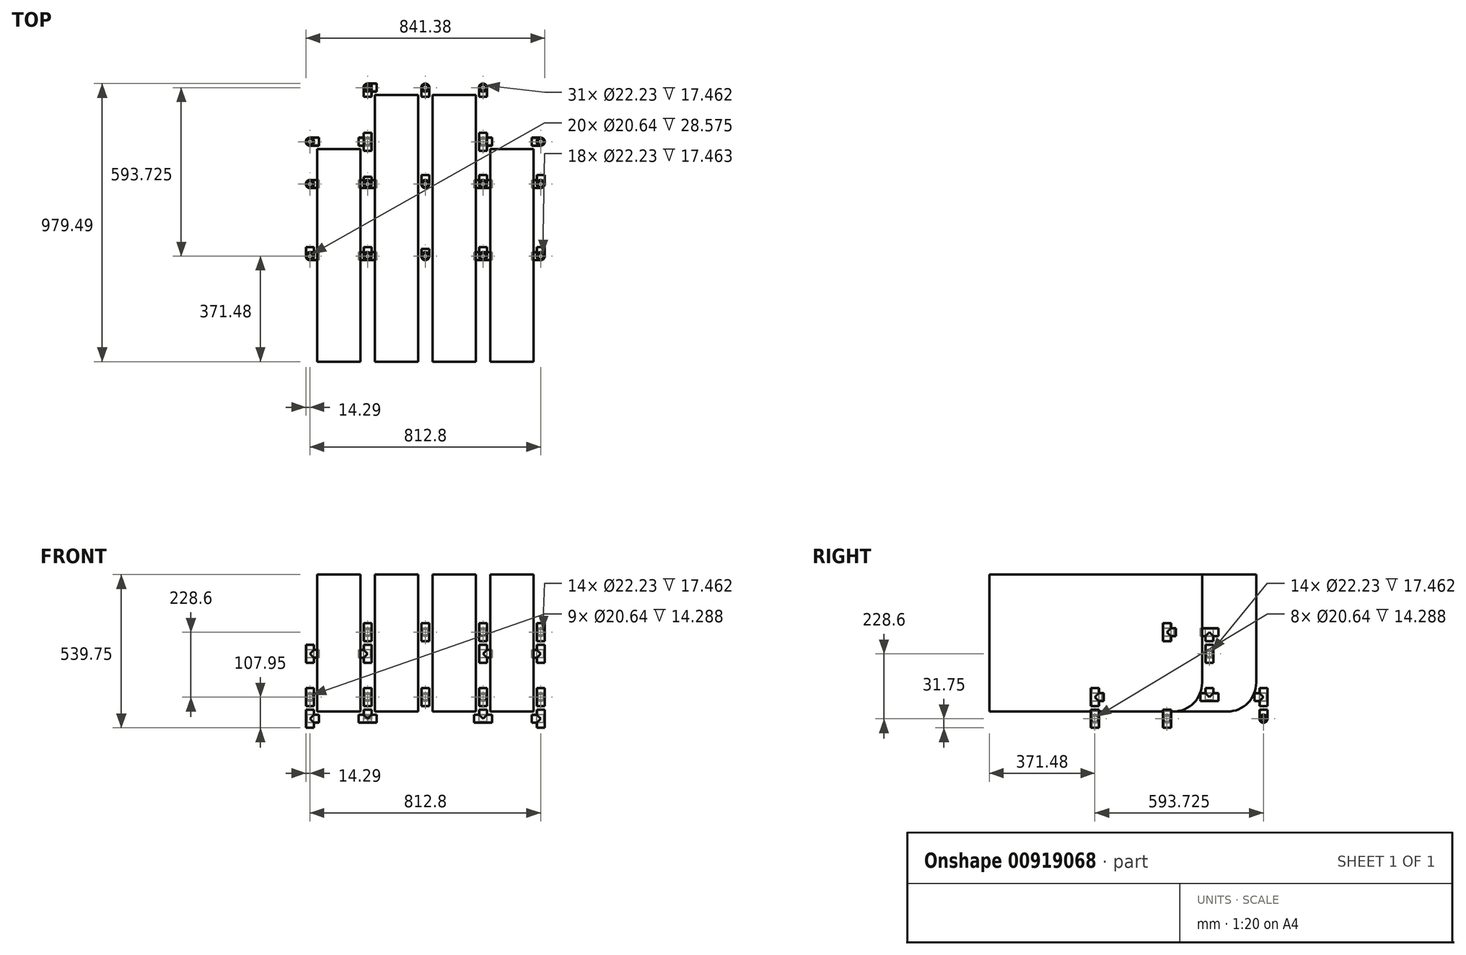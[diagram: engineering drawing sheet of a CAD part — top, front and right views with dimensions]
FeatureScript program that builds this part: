
annotation { "Feature Type Name" : "Feature", "Feature Type Description" : "" }
export const myFeature = defineFeature(function(context is Context, id is Id, definition is map)
    precondition{}
    {
        {
            var Q0;
            Q0=qCreatedBy(makeId("Front.planeOp"),FACE);
            var sketch = newSketch(context, id + "F0", { "sketchPlane" : qUnion([Q0])});
            skLineSegment(sketch, "E0", {"start": v(0, 0) * mm, "end": v(0, 76.2) * mm, "construction": true});
            skLineSegment(sketch, "E1", {"start": v(0, 76.2) * mm, "end": v(0, 381) * mm, "construction": true});
            skLineSegment(sketch, "E2", {"start": v(203.2, 0) * mm, "end": v(203.2, 76.2) * mm, "construction": true});
            skLineSegment(sketch, "E3", {"start": v(203.2, 76.2) * mm, "end": v(203.2, 381) * mm, "construction": true});
            skLineSegment(sketch, "E4", {"start": v(203.2, 381) * mm, "end": v(203.2, 381) * mm});
            skLineSegment(sketch, "E5", {"start": v(406.4, 0) * mm, "end": v(406.4, 76.2) * mm, "construction": true});
            skLineSegment(sketch, "E6", {"start": v(406.4, 76.2) * mm, "end": v(406.4, 381) * mm, "construction": true});
            skLineSegment(sketch, "E7", {"start": v(609.6, 0) * mm, "end": v(609.6, 76.2) * mm, "construction": true});
            skLineSegment(sketch, "E8", {"start": v(609.6, 76.2) * mm, "end": v(609.6, 381) * mm, "construction": true});
            skLineSegment(sketch, "E9", {"start": v(609.6, 381) * mm, "end": v(609.6, 381) * mm});
            skLineSegment(sketch, "E10", {"start": v(812.8, 0) * mm, "end": v(812.8, 76.2) * mm, "construction": true});
            skLineSegment(sketch, "E11", {"start": v(812.8, 76.2) * mm, "end": v(812.8, 381) * mm, "construction": true});
            skLineSegment(sketch, "E12", {"start": v(0, 0) * mm, "end": v(203.2, 0) * mm, "construction": true});
            skLineSegment(sketch, "E13", {"start": v(406.4, 0) * mm, "end": v(609.6, 0) * mm, "construction": true});
            skLineSegment(sketch, "E14", {"start": v(812.8, 0) * mm, "end": v(609.6, 0) * mm, "construction": true});
            skLineSegment(sketch, "E15", {"start": v(406.4, 0) * mm, "end": v(203.2, 0) * mm, "construction": true});
            skCircle(sketch, "E16", {"center": v(406.4, 381) * mm, "radius": 14.29 * mm});
            skCircle(sketch, "E17", {"center": v(406.4, 381) * mm, "radius": 11.11 * mm});
            skCircle(sketch, "E18", {"center": v(406.4, 381) * mm, "radius": 10.32 * mm});
            skCircle(sketch, "E19", {"center": v(406.4, 381) * mm, "radius": 25.4 * mm});
            skCircle(sketch, "E20", {"center": v(609.6, 381) * mm, "radius": 14.29 * mm});
            skCircle(sketch, "E21", {"center": v(609.6, 381) * mm, "radius": 11.11 * mm});
            skCircle(sketch, "E22", {"center": v(609.6, 381) * mm, "radius": 10.32 * mm});
            skCircle(sketch, "E23", {"center": v(609.6, 381) * mm, "radius": 25.4 * mm});
            skCircle(sketch, "E24", {"center": v(203.2, 381) * mm, "radius": 14.29 * mm});
            skCircle(sketch, "E25", {"center": v(203.2, 381) * mm, "radius": 11.11 * mm});
            skCircle(sketch, "E26", {"center": v(203.2, 381) * mm, "radius": 10.32 * mm});
            skCircle(sketch, "E27", {"center": v(203.2, 381) * mm, "radius": 25.4 * mm});
            skCircle(sketch, "E28", {"center": v(406.4, 76.2) * mm, "radius": 14.29 * mm});
            skCircle(sketch, "E29", {"center": v(406.4, 76.2) * mm, "radius": 11.11 * mm});
            skCircle(sketch, "E30", {"center": v(406.4, 76.2) * mm, "radius": 10.32 * mm});
            skCircle(sketch, "E31", {"center": v(406.4, 76.2) * mm, "radius": 25.4 * mm});
            skCircle(sketch, "E32", {"center": v(0, 76.2) * mm, "radius": 14.29 * mm});
            skCircle(sketch, "E33", {"center": v(0, 76.2) * mm, "radius": 11.11 * mm});
            skCircle(sketch, "E34", {"center": v(0, 76.2) * mm, "radius": 10.32 * mm});
            skCircle(sketch, "E35", {"center": v(0, 76.2) * mm, "radius": 25.4 * mm});
            skCircle(sketch, "E36", {"center": v(812.8, 381) * mm, "radius": 14.29 * mm});
            skCircle(sketch, "E37", {"center": v(812.8, 381) * mm, "radius": 11.11 * mm});
            skCircle(sketch, "E38", {"center": v(812.8, 381) * mm, "radius": 10.32 * mm});
            skCircle(sketch, "E39", {"center": v(812.8, 381) * mm, "radius": 25.4 * mm});
            skCircle(sketch, "E40", {"center": v(812.8, 76.2) * mm, "radius": 14.29 * mm});
            skCircle(sketch, "E41", {"center": v(812.8, 76.2) * mm, "radius": 11.11 * mm});
            skCircle(sketch, "E42", {"center": v(812.8, 76.2) * mm, "radius": 10.32 * mm});
            skCircle(sketch, "E43", {"center": v(812.8, 76.2) * mm, "radius": 25.4 * mm});
            skCircle(sketch, "E44", {"center": v(0, 381) * mm, "radius": 14.29 * mm});
            skCircle(sketch, "E45", {"center": v(0, 381) * mm, "radius": 11.11 * mm});
            skCircle(sketch, "E46", {"center": v(0, 381) * mm, "radius": 10.32 * mm});
            skCircle(sketch, "E47", {"center": v(0, 381) * mm, "radius": 25.4 * mm});
            skCircle(sketch, "E48", {"center": v(609.6, 76.2) * mm, "radius": 14.29 * mm});
            skCircle(sketch, "E49", {"center": v(609.6, 76.2) * mm, "radius": 11.11 * mm});
            skCircle(sketch, "E50", {"center": v(609.6, 76.2) * mm, "radius": 10.32 * mm});
            skCircle(sketch, "E51", {"center": v(609.6, 76.2) * mm, "radius": 25.4 * mm});
            skCircle(sketch, "E52", {"center": v(203.2, 76.2) * mm, "radius": 14.29 * mm});
            skCircle(sketch, "E53", {"center": v(203.2, 76.2) * mm, "radius": 11.11 * mm});
            skCircle(sketch, "E54", {"center": v(203.2, 76.2) * mm, "radius": 10.32 * mm});
            skCircle(sketch, "E55", {"center": v(203.2, 76.2) * mm, "radius": 25.4 * mm});
            skSolve(sketch);
        }
        {
            var Q0;
            Q0=qCreatedBy(makeId("Right.planeOp"),FACE);
            var sketch = newSketch(context, id + "F1", { "sketchPlane" : qUnion([Q0])});
            skLineSegment(sketch, "E56", {"start": v(254, 0) * mm, "end": v(254, 76.2) * mm, "construction": true});
            skLineSegment(sketch, "E57", {"start": v(254, 76.2) * mm, "end": v(254, 304.8) * mm, "construction": true});
            skLineSegment(sketch, "E58", {"start": v(254, 304.8) * mm, "end": v(254, 381) * mm, "construction": true});
            skLineSegment(sketch, "E59", {"start": v(254, 381) * mm, "end": v(254, 381) * mm});
            skLineSegment(sketch, "E60", {"start": v(403.23, 0) * mm, "end": v(403.23, 76.2) * mm, "construction": true});
            skLineSegment(sketch, "E61", {"start": v(403.23, 76.2) * mm, "end": v(403.23, 228.6) * mm, "construction": true});
            skLineSegment(sketch, "E62", {"start": v(403.23, 228.6) * mm, "end": v(403.23, 304.8) * mm, "construction": true});
            skCircle(sketch, "E63", {"center": v(0, 0) * mm, "radius": 14.29 * mm});
            skCircle(sketch, "E64", {"center": v(0, 0) * mm, "radius": 11.11 * mm});
            skCircle(sketch, "E65", {"center": v(0, 0) * mm, "radius": 10.32 * mm});
            skLineSegment(sketch, "E66", {"start": v(0, 0) * mm, "end": v(0, 76.2) * mm, "construction": true});
            skLineSegment(sketch, "E67", {"start": v(0, 76.2) * mm, "end": v(0, 381) * mm, "construction": true});
            skCircle(sketch, "E68", {"center": v(403.23, 228.6) * mm, "radius": 14.29 * mm});
            skCircle(sketch, "E69", {"center": v(403.23, 228.6) * mm, "radius": 11.11 * mm});
            skCircle(sketch, "E70", {"center": v(403.23, 228.6) * mm, "radius": 10.32 * mm});
            skCircle(sketch, "E71", {"center": v(403.23, 228.6) * mm, "radius": 25.4 * mm});
            skCircle(sketch, "E72", {"center": v(0, 0) * mm, "radius": 25.4 * mm});
            skCircle(sketch, "E73.1.0.0", {"center": v(254, 0) * mm, "radius": 25.4 * mm});
            skCircle(sketch, "E73.1.0.1", {"center": v(254, 0) * mm, "radius": 11.11 * mm});
            skCircle(sketch, "E73.1.0.2", {"center": v(254, 0) * mm, "radius": 10.32 * mm});
            skCircle(sketch, "E73.1.0.3", {"center": v(254, 0) * mm, "radius": 14.29 * mm});
            skLineSegment(sketch, "E73.direction1", {"start": v(0, 0) * mm, "end": v(254, 0) * mm, "construction": true});
            skLineSegment(sketch, "E74", {"start": v(0, 76.2) * mm, "end": v(254, 76.2) * mm, "construction": true});
            skLineSegment(sketch, "E75", {"start": v(0, 381) * mm, "end": v(254, 381) * mm, "construction": true});
            skLineSegment(sketch, "E76", {"start": v(254, 304.8) * mm, "end": v(403.23, 304.8) * mm, "construction": true});
            skLineSegment(sketch, "E77", {"start": v(254, 76.2) * mm, "end": v(403.23, 76.2) * mm, "construction": true});
            skSolve(sketch);
        }
        {
            var Q0;
            Q0=qCreatedBy(makeId("Right.planeOp"),FACE);
            cPlane(context, id + "F2", {"entities" : qUnion([Q0]), "cplaneType" : CPlaneType.OFFSET, "offset" : 101.6 * mm, "width" : 152.4 * mm, "height" : 152.4 * mm});
        }
        {
            var Q0;
            Q0=qCreatedBy(id+"F2.planeOp",FACE);
            var sketch = newSketch(context, id + "F3", { "sketchPlane" : qUnion([Q0])});
            skLineSegment(sketch, "E78.bottom", {"start": v(377.82, 508) * mm, "end": v(-371.48, 508) * mm});
            skLineSegment(sketch, "E78.top", {"start": v(276.23, 25.4) * mm, "end": v(-371.48, 25.4) * mm});
            skLineSegment(sketch, "E78.left", {"start": v(377.82, 508) * mm, "end": v(377.83, 127) * mm});
            skLineSegment(sketch, "E78.right", {"start": v(-371.48, 508) * mm, "end": v(-371.48, 25.4) * mm});
            skPoint(sketch, "E79.visualSharp", {"position": v(377.83, 25.4) * mm});
            skArc(sketch, "E79.filletArc", {"start": v(276.23, 25.4) * mm, "mid": v(348.07, 55.16) * mm, "end": v(377.83, 127) * mm});
            skSolve(sketch);
        }
        {
            var Q0;
            Q0 = qSketchRegion(id + "F3", true);
            extrude(context, id + "F4", {"entities" : qUnion([Q0]), "endBound" : BoundingType.SYMMETRIC, "depth" : 152.4 * mm, "offsetDistance" : 25.4 * mm});
        }
        {
            var Q0;
            Q0=qCreatedBy(id+"F2.planeOp",FACE);
            cPlane(context, id + "F5", {"entities" : qUnion([Q0]), "cplaneType" : CPlaneType.OFFSET, "offset" : 203.2 * mm, "width" : 152.4 * mm, "height" : 152.4 * mm});
        }
        {
            var Q0;
            Q0=qCreatedBy(id+"F5.planeOp",FACE);
            var sketch = newSketch(context, id + "F6", { "sketchPlane" : qUnion([Q0])});
            skLineSegment(sketch, "E80.bottom", {"start": v(-371.48, 508) * mm, "end": v(568.33, 508) * mm});
            skLineSegment(sketch, "E80.top", {"start": v(-371.48, 25.4) * mm, "end": v(466.73, 25.4) * mm});
            skLineSegment(sketch, "E80.left", {"start": v(-371.48, 508) * mm, "end": v(-371.48, 25.4) * mm});
            skLineSegment(sketch, "E80.right", {"start": v(568.33, 508) * mm, "end": v(568.33, 127) * mm});
            skPoint(sketch, "E81.visualSharp", {"position": v(568.33, 25.4) * mm});
            skArc(sketch, "E81.filletArc", {"start": v(466.73, 25.4) * mm, "mid": v(538.57, 55.16) * mm, "end": v(568.33, 127) * mm});
            skSolve(sketch);
        }
        {
            var Q0;
            Q0 = qSketchRegion(id + "F6", true);
            extrude(context, id + "F7", {"entities" : qUnion([Q0]), "endBound" : BoundingType.SYMMETRIC, "depth" : 152.4 * mm, "offsetDistance" : 25.4 * mm});
        }
        {
            var Q0;
            Q0=qCreatedBy(id+"F5.planeOp",FACE);
            cPlane(context, id + "F8", {"entities" : qUnion([Q0]), "cplaneType" : CPlaneType.OFFSET, "offset" : 203.2 * mm, "width" : 152.4 * mm, "height" : 152.4 * mm});
        }
        {
            var Q0;
            Q0=qCreatedBy(id+"F8.planeOp",FACE);
            var sketch = newSketch(context, id + "F9", { "sketchPlane" : qUnion([Q0])});
            skLineSegment(sketch, "E82.bottom", {"start": v(568.32, 508) * mm, "end": v(-371.48, 508) * mm});
            skLineSegment(sketch, "E82.top", {"start": v(466.72, 25.4) * mm, "end": v(-371.48, 25.4) * mm});
            skLineSegment(sketch, "E82.left", {"start": v(568.32, 508) * mm, "end": v(568.32, 127) * mm});
            skLineSegment(sketch, "E82.right", {"start": v(-371.48, 508) * mm, "end": v(-371.48, 25.4) * mm});
            skPoint(sketch, "E83.visualSharp", {"position": v(568.32, 25.4) * mm});
            skArc(sketch, "E83.filletArc", {"start": v(466.72, 25.4) * mm, "mid": v(538.57, 55.16) * mm, "end": v(568.32, 127) * mm});
            skSolve(sketch);
        }
        {
            var Q0;
            Q0 = qSketchRegion(id + "F9", true);
            extrude(context, id + "F10", {"entities" : qUnion([Q0]), "endBound" : BoundingType.SYMMETRIC, "depth" : 152.4 * mm, "offsetDistance" : 25.4 * mm});
        }
        {
            var Q0;
            Q0=qCreatedBy(id+"F8.planeOp",FACE);
            cPlane(context, id + "F11", {"entities" : qUnion([Q0]), "cplaneType" : CPlaneType.OFFSET, "offset" : 203.2 * mm, "width" : 152.4 * mm, "height" : 152.4 * mm});
        }
        {
            var Q0;
            Q0=qCreatedBy(id+"F11.planeOp",FACE);
            var sketch = newSketch(context, id + "F12", { "sketchPlane" : qUnion([Q0])});
            skLineSegment(sketch, "E84.bottom", {"start": v(377.82, 508) * mm, "end": v(-371.48, 508) * mm});
            skLineSegment(sketch, "E84.top", {"start": v(276.22, 25.4) * mm, "end": v(-371.48, 25.4) * mm});
            skLineSegment(sketch, "E84.left", {"start": v(377.82, 508) * mm, "end": v(377.82, 127) * mm});
            skLineSegment(sketch, "E84.right", {"start": v(-371.48, 508) * mm, "end": v(-371.48, 25.4) * mm});
            skPoint(sketch, "E85.visualSharp", {"position": v(377.82, 25.4) * mm});
            skArc(sketch, "E85.filletArc", {"start": v(276.22, 25.4) * mm, "mid": v(348.07, 55.16) * mm, "end": v(377.82, 127) * mm});
            skSolve(sketch);
        }
        {
            var Q0;
            Q0 = qSketchRegion(id + "F12", true);
            extrude(context, id + "F13", {"entities" : qUnion([Q0]), "endBound" : BoundingType.SYMMETRIC, "depth" : 152.4 * mm, "offsetDistance" : 25.4 * mm});
        }
        {
            var Q0;
            Q0=qCreatedBy(makeId("Right.planeOp"),FACE);
            cPlane(context, id + "F14", {"entities" : qUnion([Q0]), "cplaneType" : CPlaneType.OFFSET, "offset" : 203.2 * mm, "width" : 152.4 * mm, "height" : 152.4 * mm});
        }
        {
            var Q0;
            Q0=qCreatedBy(id+"F14.planeOp",FACE);
            var sketch = newSketch(context, id + "F15", { "sketchPlane" : qUnion([Q0])});
            skLineSegment(sketch, "E86", {"start": v(0, 0) * mm, "end": v(0, 76.2) * mm, "construction": true});
            skLineSegment(sketch, "E87", {"start": v(0, 76.2) * mm, "end": v(0, 381) * mm, "construction": true});
            skLineSegment(sketch, "E88", {"start": v(0, 381) * mm, "end": v(0, 381) * mm});
            skLineSegment(sketch, "E89", {"start": v(254, 0) * mm, "end": v(254, 76.2) * mm, "construction": true});
            skLineSegment(sketch, "E90", {"start": v(254, 76.2) * mm, "end": v(254, 304.8) * mm, "construction": true});
            skLineSegment(sketch, "E91", {"start": v(254, 304.8) * mm, "end": v(254, 381) * mm, "construction": true});
            skLineSegment(sketch, "E92", {"start": v(403.23, 0) * mm, "end": v(403.23, 76.2) * mm, "construction": true});
            skLineSegment(sketch, "E93", {"start": v(403.23, 76.2) * mm, "end": v(403.23, 304.8) * mm, "construction": true});
            skCircle(sketch, "E94", {"center": v(0, 0) * mm, "radius": 14.29 * mm});
            skCircle(sketch, "E95", {"center": v(0, 0) * mm, "radius": 11.11 * mm});
            skCircle(sketch, "E96", {"center": v(0, 0) * mm, "radius": 10.32 * mm});
            skCircle(sketch, "E97", {"center": v(0, 0) * mm, "radius": 25.4 * mm});
            skCircle(sketch, "E98", {"center": v(403.23, 228.6) * mm, "radius": 14.29 * mm});
            skCircle(sketch, "E99", {"center": v(403.23, 228.6) * mm, "radius": 11.11 * mm});
            skCircle(sketch, "E100", {"center": v(403.23, 228.6) * mm, "radius": 10.32 * mm});
            skCircle(sketch, "E101", {"center": v(403.23, 228.6) * mm, "radius": 25.4 * mm});
            skCircle(sketch, "E102", {"center": v(254, 0) * mm, "radius": 14.29 * mm});
            skCircle(sketch, "E103", {"center": v(254, 0) * mm, "radius": 11.11 * mm});
            skCircle(sketch, "E104", {"center": v(254, 0) * mm, "radius": 10.32 * mm});
            skCircle(sketch, "E105", {"center": v(254, 0) * mm, "radius": 25.4 * mm});
            skLineSegment(sketch, "E106", {"start": v(593.73, 0) * mm, "end": v(593.73, 76.2) * mm, "construction": true});
            skLineSegment(sketch, "E107", {"start": v(593.73, 76.2) * mm, "end": v(593.73, 228.6) * mm, "construction": true});
            skLineSegment(sketch, "E108", {"start": v(593.73, 228.6) * mm, "end": v(593.73, 304.8) * mm, "construction": true});
            skCircle(sketch, "E109", {"center": v(593.73, 228.6) * mm, "radius": 14.29 * mm});
            skCircle(sketch, "E110", {"center": v(593.73, 228.6) * mm, "radius": 11.11 * mm});
            skCircle(sketch, "E111", {"center": v(593.73, 228.6) * mm, "radius": 10.32 * mm});
            skCircle(sketch, "E112", {"center": v(593.73, 228.6) * mm, "radius": 25.4 * mm});
            skCircle(sketch, "E113", {"center": v(593.73, 0) * mm, "radius": 14.29 * mm});
            skCircle(sketch, "E114", {"center": v(593.73, 0) * mm, "radius": 11.11 * mm});
            skCircle(sketch, "E115", {"center": v(593.73, 0) * mm, "radius": 10.32 * mm});
            skCircle(sketch, "E116", {"center": v(593.73, 0) * mm, "radius": 25.4 * mm});
            skSolve(sketch);
        }
        {
            var Q0;
            Q0=qCreatedBy(id+"F14.planeOp",FACE);
            cPlane(context, id + "F16", {"entities" : qUnion([Q0]), "cplaneType" : CPlaneType.OFFSET, "offset" : 203.2 * mm, "width" : 152.4 * mm, "height" : 152.4 * mm});
        }
        {
            var Q0;
            Q0=qCreatedBy(id+"F16.planeOp",FACE);
            cPlane(context, id + "F17", {"entities" : qUnion([Q0]), "cplaneType" : CPlaneType.OFFSET, "offset" : 203.2 * mm, "width" : 152.4 * mm, "height" : 152.4 * mm});
        }
        {
            var Q0;
            Q0=qCreatedBy(id+"F17.planeOp",FACE);
            var sketch = newSketch(context, id + "F18", { "sketchPlane" : qUnion([Q0])});
            skLineSegment(sketch, "E117", {"start": v(0, 0) * mm, "end": v(0, 76.2) * mm, "construction": true});
            skLineSegment(sketch, "E118", {"start": v(0, 76.2) * mm, "end": v(0, 381) * mm, "construction": true});
            skLineSegment(sketch, "E119", {"start": v(254, 0) * mm, "end": v(254, 76.2) * mm, "construction": true});
            skLineSegment(sketch, "E120", {"start": v(254, 76.2) * mm, "end": v(254, 304.8) * mm, "construction": true});
            skLineSegment(sketch, "E121", {"start": v(254, 304.8) * mm, "end": v(254, 381) * mm, "construction": true});
            skLineSegment(sketch, "E122", {"start": v(403.23, 0) * mm, "end": v(403.23, 76.2) * mm, "construction": true});
            skLineSegment(sketch, "E123", {"start": v(403.23, 76.2) * mm, "end": v(403.23, 228.6) * mm, "construction": true});
            skLineSegment(sketch, "E124", {"start": v(403.23, 228.6) * mm, "end": v(403.23, 304.8) * mm, "construction": true});
            skLineSegment(sketch, "E125", {"start": v(403.23, 304.8) * mm, "end": v(403.23, 304.8) * mm});
            skLineSegment(sketch, "E126", {"start": v(593.73, 0) * mm, "end": v(593.73, 76.2) * mm, "construction": true});
            skLineSegment(sketch, "E127", {"start": v(593.73, 76.2) * mm, "end": v(593.73, 228.6) * mm, "construction": true});
            skLineSegment(sketch, "E128", {"start": v(593.73, 228.6) * mm, "end": v(593.73, 304.8) * mm, "construction": true});
            skCircle(sketch, "E129", {"center": v(403.23, 228.6) * mm, "radius": 14.29 * mm});
            skCircle(sketch, "E130", {"center": v(403.23, 228.6) * mm, "radius": 11.11 * mm});
            skCircle(sketch, "E131", {"center": v(403.23, 228.6) * mm, "radius": 10.32 * mm});
            skCircle(sketch, "E132", {"center": v(403.23, 228.6) * mm, "radius": 25.4 * mm});
            skCircle(sketch, "E133", {"center": v(593.73, 228.6) * mm, "radius": 14.29 * mm});
            skCircle(sketch, "E134", {"center": v(593.73, 228.6) * mm, "radius": 11.11 * mm});
            skCircle(sketch, "E135", {"center": v(593.73, 228.6) * mm, "radius": 10.32 * mm});
            skCircle(sketch, "E136", {"center": v(593.73, 228.6) * mm, "radius": 25.4 * mm});
            skCircle(sketch, "E137", {"center": v(254, 0) * mm, "radius": 14.29 * mm});
            skCircle(sketch, "E138", {"center": v(254, 0) * mm, "radius": 11.11 * mm});
            skCircle(sketch, "E139", {"center": v(254, 0) * mm, "radius": 10.32 * mm});
            skCircle(sketch, "E140", {"center": v(254, 0) * mm, "radius": 25.4 * mm});
            skCircle(sketch, "E141", {"center": v(0, 0) * mm, "radius": 14.29 * mm});
            skCircle(sketch, "E142", {"center": v(0, 0) * mm, "radius": 11.11 * mm});
            skCircle(sketch, "E143", {"center": v(0, 0) * mm, "radius": 10.32 * mm});
            skCircle(sketch, "E144", {"center": v(0, 0) * mm, "radius": 25.4 * mm});
            skCircle(sketch, "E145", {"center": v(593.73, 0) * mm, "radius": 14.29 * mm});
            skCircle(sketch, "E146", {"center": v(593.73, 0) * mm, "radius": 11.11 * mm});
            skCircle(sketch, "E147", {"center": v(593.73, 0) * mm, "radius": 10.32 * mm});
            skCircle(sketch, "E148", {"center": v(593.73, 0) * mm, "radius": 25.4 * mm});
            skSolve(sketch);
        }
        {
            var Q0;
            Q0=qCreatedBy(id+"F17.planeOp",FACE);
            cPlane(context, id + "F19", {"entities" : qUnion([Q0]), "cplaneType" : CPlaneType.OFFSET, "offset" : 203.2 * mm, "width" : 152.4 * mm, "height" : 152.4 * mm});
        }
        {
            var Q0;
            Q0=qCreatedBy(id+"F19.planeOp",FACE);
            var sketch = newSketch(context, id + "F20", { "sketchPlane" : qUnion([Q0])});
            skLineSegment(sketch, "E149", {"start": v(0, 0) * mm, "end": v(0, 76.2) * mm, "construction": true});
            skLineSegment(sketch, "E150", {"start": v(0, 76.2) * mm, "end": v(0, 381) * mm, "construction": true});
            skLineSegment(sketch, "E151", {"start": v(254, 0) * mm, "end": v(254, 76.2) * mm, "construction": true});
            skLineSegment(sketch, "E152", {"start": v(254, 76.2) * mm, "end": v(254, 304.8) * mm, "construction": true});
            skLineSegment(sketch, "E153", {"start": v(254, 304.8) * mm, "end": v(254, 381) * mm, "construction": true});
            skLineSegment(sketch, "E154", {"start": v(254, 381) * mm, "end": v(254, 381) * mm});
            skLineSegment(sketch, "E155", {"start": v(403.23, 0) * mm, "end": v(403.23, 76.2) * mm, "construction": true});
            skLineSegment(sketch, "E156", {"start": v(403.23, 76.2) * mm, "end": v(403.23, 228.6) * mm, "construction": true});
            skLineSegment(sketch, "E157", {"start": v(403.23, 228.6) * mm, "end": v(403.23, 304.8) * mm, "construction": true});
            skCircle(sketch, "E158", {"center": v(0, 0) * mm, "radius": 14.29 * mm});
            skCircle(sketch, "E159", {"center": v(0, 0) * mm, "radius": 11.11 * mm});
            skCircle(sketch, "E160", {"center": v(0, 0) * mm, "radius": 10.32 * mm});
            skCircle(sketch, "E161", {"center": v(0, 0) * mm, "radius": 25.4 * mm});
            skCircle(sketch, "E162", {"center": v(403.23, 228.6) * mm, "radius": 14.29 * mm});
            skCircle(sketch, "E163", {"center": v(403.23, 228.6) * mm, "radius": 11.11 * mm});
            skCircle(sketch, "E164", {"center": v(403.23, 228.6) * mm, "radius": 10.32 * mm});
            skCircle(sketch, "E165", {"center": v(403.23, 228.6) * mm, "radius": 25.4 * mm});
            skCircle(sketch, "E166", {"center": v(254, 0) * mm, "radius": 14.29 * mm});
            skCircle(sketch, "E167", {"center": v(254, 0) * mm, "radius": 11.11 * mm});
            skCircle(sketch, "E168", {"center": v(254, 0) * mm, "radius": 10.32 * mm});
            skCircle(sketch, "E169", {"center": v(254, 0) * mm, "radius": 25.4 * mm});
            skSolve(sketch);
        }
        {
            var Q0;
            Q0=qCreatedBy(makeId("Front.planeOp"),FACE);
            cPlane(context, id + "F21", {"entities" : qUnion([Q0]), "cplaneType" : CPlaneType.OFFSET, "offset" : 254 * mm, "oppositeDirection" : true, "width" : 152.4 * mm, "height" : 152.4 * mm});
        }
        {
            var Q0;
            Q0=qCreatedBy(id+"F21.planeOp",FACE);
            var sketch = newSketch(context, id + "F22", { "sketchPlane" : qUnion([Q0])});
            skLineSegment(sketch, "E170", {"start": v(0, 0) * mm, "end": v(0, 76.2) * mm, "construction": true});
            skLineSegment(sketch, "E171", {"start": v(0, 76.2) * mm, "end": v(0, 304.8) * mm, "construction": true});
            skLineSegment(sketch, "E172", {"start": v(0, 304.8) * mm, "end": v(0, 381) * mm, "construction": true});
            skLineSegment(sketch, "E173", {"start": v(0, 381) * mm, "end": v(0, 381) * mm});
            skLineSegment(sketch, "E174", {"start": v(203.2, 0) * mm, "end": v(203.2, 76.2) * mm, "construction": true});
            skLineSegment(sketch, "E175", {"start": v(203.2, 76.2) * mm, "end": v(203.2, 304.8) * mm, "construction": true});
            skLineSegment(sketch, "E176", {"start": v(203.2, 304.8) * mm, "end": v(203.2, 381) * mm, "construction": true});
            skLineSegment(sketch, "E177", {"start": v(406.4, 0) * mm, "end": v(406.4, 76.2) * mm, "construction": true});
            skLineSegment(sketch, "E178", {"start": v(406.4, 76.2) * mm, "end": v(406.4, 304.8) * mm, "construction": true});
            skLineSegment(sketch, "E179", {"start": v(406.4, 304.8) * mm, "end": v(406.4, 381) * mm, "construction": true});
            skLineSegment(sketch, "E180", {"start": v(609.6, 0) * mm, "end": v(609.6, 76.2) * mm, "construction": true});
            skLineSegment(sketch, "E181", {"start": v(609.6, 76.2) * mm, "end": v(609.6, 304.8) * mm, "construction": true});
            skLineSegment(sketch, "E182", {"start": v(609.6, 304.8) * mm, "end": v(609.6, 381) * mm, "construction": true});
            skLineSegment(sketch, "E183", {"start": v(812.8, 0) * mm, "end": v(812.8, 76.2) * mm, "construction": true});
            skLineSegment(sketch, "E184", {"start": v(812.8, 76.2) * mm, "end": v(812.8, 304.8) * mm, "construction": true});
            skLineSegment(sketch, "E185", {"start": v(812.8, 304.8) * mm, "end": v(812.8, 381) * mm, "construction": true});
            skCircle(sketch, "E186", {"center": v(406.4, 304.8) * mm, "radius": 14.29 * mm});
            skCircle(sketch, "E187", {"center": v(406.4, 304.8) * mm, "radius": 11.11 * mm});
            skCircle(sketch, "E188", {"center": v(406.4, 304.8) * mm, "radius": 10.32 * mm});
            skCircle(sketch, "E189", {"center": v(406.4, 304.8) * mm, "radius": 25.4 * mm});
            skCircle(sketch, "E190", {"center": v(0, 304.8) * mm, "radius": 14.29 * mm});
            skCircle(sketch, "E191", {"center": v(0, 304.8) * mm, "radius": 11.11 * mm});
            skCircle(sketch, "E192", {"center": v(0, 304.8) * mm, "radius": 10.32 * mm});
            skCircle(sketch, "E193", {"center": v(0, 304.8) * mm, "radius": 25.4 * mm});
            skCircle(sketch, "E194", {"center": v(406.4, 381) * mm, "radius": 14.29 * mm});
            skCircle(sketch, "E195", {"center": v(406.4, 381) * mm, "radius": 11.11 * mm});
            skCircle(sketch, "E196", {"center": v(406.4, 381) * mm, "radius": 10.32 * mm});
            skCircle(sketch, "E197", {"center": v(406.4, 381) * mm, "radius": 25.4 * mm});
            skCircle(sketch, "E198", {"center": v(812.8, 381) * mm, "radius": 14.29 * mm});
            skCircle(sketch, "E199", {"center": v(812.8, 381) * mm, "radius": 11.11 * mm});
            skCircle(sketch, "E200", {"center": v(812.8, 381) * mm, "radius": 10.32 * mm});
            skCircle(sketch, "E201", {"center": v(812.8, 381) * mm, "radius": 25.4 * mm});
            skCircle(sketch, "E202", {"center": v(203.2, 381) * mm, "radius": 14.29 * mm});
            skCircle(sketch, "E203", {"center": v(203.2, 381) * mm, "radius": 11.11 * mm});
            skCircle(sketch, "E204", {"center": v(203.2, 381) * mm, "radius": 10.32 * mm});
            skCircle(sketch, "E205", {"center": v(203.2, 381) * mm, "radius": 25.4 * mm});
            skCircle(sketch, "E206", {"center": v(0, 381) * mm, "radius": 14.29 * mm});
            skCircle(sketch, "E207", {"center": v(0, 381) * mm, "radius": 11.11 * mm});
            skCircle(sketch, "E208", {"center": v(0, 381) * mm, "radius": 10.32 * mm});
            skCircle(sketch, "E209", {"center": v(0, 381) * mm, "radius": 25.4 * mm});
            skCircle(sketch, "E210", {"center": v(812.8, 76.2) * mm, "radius": 14.29 * mm});
            skCircle(sketch, "E211", {"center": v(812.8, 76.2) * mm, "radius": 11.11 * mm});
            skCircle(sketch, "E212", {"center": v(812.8, 76.2) * mm, "radius": 10.32 * mm});
            skCircle(sketch, "E213", {"center": v(812.8, 76.2) * mm, "radius": 25.4 * mm});
            skCircle(sketch, "E214", {"center": v(609.6, 381) * mm, "radius": 14.29 * mm});
            skCircle(sketch, "E215", {"center": v(609.6, 381) * mm, "radius": 11.11 * mm});
            skCircle(sketch, "E216", {"center": v(609.6, 381) * mm, "radius": 10.32 * mm});
            skCircle(sketch, "E217", {"center": v(609.6, 381) * mm, "radius": 25.4 * mm});
            skCircle(sketch, "E218", {"center": v(203.2, 76.2) * mm, "radius": 14.29 * mm});
            skCircle(sketch, "E219", {"center": v(203.2, 76.2) * mm, "radius": 11.11 * mm});
            skCircle(sketch, "E220", {"center": v(203.2, 76.2) * mm, "radius": 10.32 * mm});
            skCircle(sketch, "E221", {"center": v(203.2, 76.2) * mm, "radius": 25.4 * mm});
            skCircle(sketch, "E222", {"center": v(609.6, 76.2) * mm, "radius": 14.29 * mm});
            skCircle(sketch, "E223", {"center": v(609.6, 76.2) * mm, "radius": 11.11 * mm});
            skCircle(sketch, "E224", {"center": v(609.6, 76.2) * mm, "radius": 10.32 * mm});
            skCircle(sketch, "E225", {"center": v(609.6, 76.2) * mm, "radius": 25.4 * mm});
            skCircle(sketch, "E226", {"center": v(609.6, 304.8) * mm, "radius": 14.29 * mm});
            skCircle(sketch, "E227", {"center": v(609.6, 304.8) * mm, "radius": 11.11 * mm});
            skCircle(sketch, "E228", {"center": v(609.6, 304.8) * mm, "radius": 10.32 * mm});
            skCircle(sketch, "E229", {"center": v(609.6, 304.8) * mm, "radius": 25.4 * mm});
            skCircle(sketch, "E230", {"center": v(203.2, 304.8) * mm, "radius": 14.29 * mm});
            skCircle(sketch, "E231", {"center": v(203.2, 304.8) * mm, "radius": 11.11 * mm});
            skCircle(sketch, "E232", {"center": v(203.2, 304.8) * mm, "radius": 10.32 * mm});
            skCircle(sketch, "E233", {"center": v(203.2, 304.8) * mm, "radius": 25.4 * mm});
            skCircle(sketch, "E234", {"center": v(406.4, 76.2) * mm, "radius": 14.29 * mm});
            skCircle(sketch, "E235", {"center": v(406.4, 76.2) * mm, "radius": 11.11 * mm});
            skCircle(sketch, "E236", {"center": v(406.4, 76.2) * mm, "radius": 10.32 * mm});
            skCircle(sketch, "E237", {"center": v(406.4, 76.2) * mm, "radius": 25.4 * mm});
            skCircle(sketch, "E238", {"center": v(0, 76.2) * mm, "radius": 14.29 * mm});
            skCircle(sketch, "E239", {"center": v(0, 76.2) * mm, "radius": 11.11 * mm});
            skCircle(sketch, "E240", {"center": v(0, 76.2) * mm, "radius": 10.32 * mm});
            skCircle(sketch, "E241", {"center": v(0, 76.2) * mm, "radius": 25.4 * mm});
            skCircle(sketch, "E242", {"center": v(812.8, 304.8) * mm, "radius": 14.29 * mm});
            skCircle(sketch, "E243", {"center": v(812.8, 304.8) * mm, "radius": 11.11 * mm});
            skCircle(sketch, "E244", {"center": v(812.8, 304.8) * mm, "radius": 10.32 * mm});
            skCircle(sketch, "E245", {"center": v(812.8, 304.8) * mm, "radius": 25.4 * mm});
            skSolve(sketch);
        }
        {
            var Q0;
            Q0=qCreatedBy(id+"F21.planeOp",FACE);
            cPlane(context, id + "F23", {"entities" : qUnion([Q0]), "cplaneType" : CPlaneType.OFFSET, "offset" : 149.22 * mm, "oppositeDirection" : true, "width" : 152.4 * mm, "height" : 152.4 * mm});
        }
        {
            var Q0;
            Q0=qCreatedBy(id+"F23.planeOp",FACE);
            var sketch = newSketch(context, id + "F24", { "sketchPlane" : qUnion([Q0])});
            skLineSegment(sketch, "E246", {"start": v(0, 0) * mm, "end": v(0, 76.2) * mm, "construction": true});
            skLineSegment(sketch, "E247", {"start": v(0, 76.2) * mm, "end": v(0, 228.6) * mm, "construction": true});
            skLineSegment(sketch, "E248", {"start": v(0, 228.6) * mm, "end": v(0, 304.8) * mm, "construction": true});
            skLineSegment(sketch, "E249", {"start": v(203.2, 0) * mm, "end": v(203.2, 76.2) * mm, "construction": true});
            skLineSegment(sketch, "E250", {"start": v(203.2, 76.2) * mm, "end": v(203.2, 228.6) * mm, "construction": true});
            skLineSegment(sketch, "E251", {"start": v(203.2, 228.6) * mm, "end": v(203.2, 304.8) * mm, "construction": true});
            skLineSegment(sketch, "E252", {"start": v(609.6, 0) * mm, "end": v(609.6, 76.2) * mm, "construction": true});
            skLineSegment(sketch, "E253", {"start": v(609.6, 76.2) * mm, "end": v(609.6, 228.6) * mm, "construction": true});
            skLineSegment(sketch, "E254", {"start": v(609.6, 228.6) * mm, "end": v(609.6, 304.8) * mm, "construction": true});
            skLineSegment(sketch, "E255", {"start": v(812.8, 0) * mm, "end": v(812.8, 76.2) * mm, "construction": true});
            skLineSegment(sketch, "E256", {"start": v(812.8, 76.2) * mm, "end": v(812.8, 228.6) * mm, "construction": true});
            skLineSegment(sketch, "E257", {"start": v(812.8, 228.6) * mm, "end": v(812.8, 304.8) * mm, "construction": true});
            skCircle(sketch, "E258", {"center": v(812.8, 304.8) * mm, "radius": 14.29 * mm});
            skCircle(sketch, "E259", {"center": v(812.8, 304.8) * mm, "radius": 11.11 * mm});
            skCircle(sketch, "E260", {"center": v(812.8, 304.8) * mm, "radius": 10.32 * mm});
            skCircle(sketch, "E261", {"center": v(812.8, 304.8) * mm, "radius": 25.4 * mm});
            skCircle(sketch, "E262", {"center": v(609.6, 304.8) * mm, "radius": 14.29 * mm});
            skCircle(sketch, "E263", {"center": v(609.6, 304.8) * mm, "radius": 11.11 * mm});
            skCircle(sketch, "E264", {"center": v(609.6, 304.8) * mm, "radius": 10.32 * mm});
            skCircle(sketch, "E265", {"center": v(609.6, 304.8) * mm, "radius": 25.4 * mm});
            skCircle(sketch, "E266", {"center": v(0, 76.2) * mm, "radius": 14.29 * mm});
            skCircle(sketch, "E267", {"center": v(0, 76.2) * mm, "radius": 11.11 * mm});
            skCircle(sketch, "E268", {"center": v(0, 76.2) * mm, "radius": 10.32 * mm});
            skCircle(sketch, "E269", {"center": v(0, 76.2) * mm, "radius": 25.4 * mm});
            skCircle(sketch, "E270", {"center": v(0, 304.8) * mm, "radius": 14.29 * mm});
            skCircle(sketch, "E271", {"center": v(0, 304.8) * mm, "radius": 11.11 * mm});
            skCircle(sketch, "E272", {"center": v(0, 304.8) * mm, "radius": 10.32 * mm});
            skCircle(sketch, "E273", {"center": v(0, 304.8) * mm, "radius": 25.4 * mm});
            skCircle(sketch, "E274", {"center": v(203.2, 76.2) * mm, "radius": 14.29 * mm});
            skCircle(sketch, "E275", {"center": v(203.2, 76.2) * mm, "radius": 11.11 * mm});
            skCircle(sketch, "E276", {"center": v(203.2, 76.2) * mm, "radius": 10.32 * mm});
            skCircle(sketch, "E277", {"center": v(203.2, 76.2) * mm, "radius": 25.4 * mm});
            skCircle(sketch, "E278", {"center": v(203.2, 304.8) * mm, "radius": 14.29 * mm});
            skCircle(sketch, "E279", {"center": v(203.2, 304.8) * mm, "radius": 11.11 * mm});
            skCircle(sketch, "E280", {"center": v(203.2, 304.8) * mm, "radius": 10.32 * mm});
            skCircle(sketch, "E281", {"center": v(203.2, 304.8) * mm, "radius": 25.4 * mm});
            skCircle(sketch, "E282", {"center": v(609.6, 76.2) * mm, "radius": 14.29 * mm});
            skCircle(sketch, "E283", {"center": v(609.6, 76.2) * mm, "radius": 11.11 * mm});
            skCircle(sketch, "E284", {"center": v(609.6, 76.2) * mm, "radius": 10.32 * mm});
            skCircle(sketch, "E285", {"center": v(609.6, 76.2) * mm, "radius": 25.4 * mm});
            skCircle(sketch, "E286", {"center": v(812.8, 76.2) * mm, "radius": 14.29 * mm});
            skCircle(sketch, "E287", {"center": v(812.8, 76.2) * mm, "radius": 11.11 * mm});
            skCircle(sketch, "E288", {"center": v(812.8, 76.2) * mm, "radius": 10.32 * mm});
            skCircle(sketch, "E289", {"center": v(812.8, 76.2) * mm, "radius": 25.4 * mm});
            skPoint(sketch, "E290.center.orphan", {"position": v(203.2, 228.6) * mm});
            skPoint(sketch, "E291.center.orphan", {"position": v(609.6, 228.6) * mm});
            skPoint(sketch, "E292.center.orphan", {"position": v(812.8, 228.6) * mm});
            skPoint(sketch, "E293.center.orphan", {"position": v(0, 228.6) * mm});
            skSolve(sketch);
        }
        {
            var Q0;
            Q0=qCreatedBy(makeId("Front.planeOp"),FACE);
            cPlane(context, id + "F25", {"entities" : qUnion([Q0]), "cplaneType" : CPlaneType.OFFSET, "offset" : 593.73 * mm, "oppositeDirection" : true, "width" : 152.4 * mm, "height" : 152.4 * mm});
        }
        {
            var Q0;
            Q0=qCreatedBy(id+"F25.planeOp",FACE);
            var sketch = newSketch(context, id + "F26", { "sketchPlane" : qUnion([Q0])});
            skLineSegment(sketch, "E294", {"start": v(203.2, 0) * mm, "end": v(203.2, 76.2) * mm, "construction": true});
            skLineSegment(sketch, "E295", {"start": v(203.2, 76.2) * mm, "end": v(203.2, 228.6) * mm, "construction": true});
            skLineSegment(sketch, "E296", {"start": v(203.2, 228.6) * mm, "end": v(203.2, 304.8) * mm, "construction": true});
            skLineSegment(sketch, "E297", {"start": v(406.4, 0) * mm, "end": v(406.4, 76.2) * mm, "construction": true});
            skLineSegment(sketch, "E298", {"start": v(406.4, 76.2) * mm, "end": v(406.4, 228.6) * mm, "construction": true});
            skLineSegment(sketch, "E299", {"start": v(406.4, 228.6) * mm, "end": v(406.4, 304.8) * mm, "construction": true});
            skLineSegment(sketch, "E300", {"start": v(609.6, 0) * mm, "end": v(609.6, 76.2) * mm, "construction": true});
            skLineSegment(sketch, "E301", {"start": v(609.6, 76.2) * mm, "end": v(609.6, 228.6) * mm, "construction": true});
            skLineSegment(sketch, "E302", {"start": v(609.6, 228.6) * mm, "end": v(609.6, 304.8) * mm, "construction": true});
            skCircle(sketch, "E303", {"center": v(609.6, 76.2) * mm, "radius": 14.29 * mm});
            skCircle(sketch, "E304", {"center": v(609.6, 76.2) * mm, "radius": 11.11 * mm});
            skCircle(sketch, "E305", {"center": v(609.6, 76.2) * mm, "radius": 10.32 * mm});
            skCircle(sketch, "E306", {"center": v(609.6, 76.2) * mm, "radius": 25.4 * mm});
            skCircle(sketch, "E307", {"center": v(406.4, 304.8) * mm, "radius": 14.29 * mm});
            skCircle(sketch, "E308", {"center": v(406.4, 304.8) * mm, "radius": 11.11 * mm});
            skCircle(sketch, "E309", {"center": v(406.4, 304.8) * mm, "radius": 10.32 * mm});
            skCircle(sketch, "E310", {"center": v(406.4, 304.8) * mm, "radius": 25.4 * mm});
            skCircle(sketch, "E311", {"center": v(203.2, 76.2) * mm, "radius": 14.29 * mm});
            skCircle(sketch, "E312", {"center": v(203.2, 76.2) * mm, "radius": 11.11 * mm});
            skCircle(sketch, "E313", {"center": v(203.2, 76.2) * mm, "radius": 10.32 * mm});
            skCircle(sketch, "E314", {"center": v(203.2, 76.2) * mm, "radius": 25.4 * mm});
            skCircle(sketch, "E315", {"center": v(406.4, 76.2) * mm, "radius": 14.29 * mm});
            skCircle(sketch, "E316", {"center": v(406.4, 76.2) * mm, "radius": 11.11 * mm});
            skCircle(sketch, "E317", {"center": v(406.4, 76.2) * mm, "radius": 10.32 * mm});
            skCircle(sketch, "E318", {"center": v(406.4, 76.2) * mm, "radius": 25.4 * mm});
            skCircle(sketch, "E319", {"center": v(609.6, 304.8) * mm, "radius": 14.29 * mm});
            skCircle(sketch, "E320", {"center": v(609.6, 304.8) * mm, "radius": 11.11 * mm});
            skCircle(sketch, "E321", {"center": v(609.6, 304.8) * mm, "radius": 10.32 * mm});
            skCircle(sketch, "E322", {"center": v(609.6, 304.8) * mm, "radius": 25.4 * mm});
            skCircle(sketch, "E323", {"center": v(203.2, 304.8) * mm, "radius": 14.29 * mm});
            skCircle(sketch, "E324", {"center": v(203.2, 304.8) * mm, "radius": 11.11 * mm});
            skCircle(sketch, "E325", {"center": v(203.2, 304.8) * mm, "radius": 10.32 * mm});
            skCircle(sketch, "E326", {"center": v(203.2, 304.8) * mm, "radius": 25.4 * mm});
            skSolve(sketch);
        }
        {
            var Q0;
            Q0=qCreatedBy(makeId("Top.planeOp"),FACE);
            var sketch = newSketch(context, id + "F27", { "sketchPlane" : qUnion([Q0])});
            skLineSegment(sketch, "E327", {"start": v(0, 0) * mm, "end": v(203.2, 0) * mm, "construction": true});
            skLineSegment(sketch, "E328", {"start": v(203.2, 0) * mm, "end": v(406.4, 0) * mm, "construction": true});
            skLineSegment(sketch, "E329", {"start": v(406.4, 0) * mm, "end": v(609.6, 0) * mm, "construction": true});
            skLineSegment(sketch, "E330", {"start": v(609.6, 0) * mm, "end": v(812.8, 0) * mm, "construction": true});
            skLineSegment(sketch, "E331", {"start": v(0, 254) * mm, "end": v(203.2, 254) * mm, "construction": true});
            skLineSegment(sketch, "E332", {"start": v(203.2, 254) * mm, "end": v(406.4, 254) * mm, "construction": true});
            skLineSegment(sketch, "E333", {"start": v(406.4, 254) * mm, "end": v(609.6, 254) * mm, "construction": true});
            skLineSegment(sketch, "E334", {"start": v(609.6, 254) * mm, "end": v(812.8, 254) * mm, "construction": true});
            skLineSegment(sketch, "E335", {"start": v(0, 403.23) * mm, "end": v(203.2, 403.23) * mm, "construction": true});
            skLineSegment(sketch, "E336", {"start": v(203.2, 403.23) * mm, "end": v(406.4, 403.23) * mm, "construction": true});
            skLineSegment(sketch, "E337", {"start": v(406.4, 403.23) * mm, "end": v(609.6, 403.23) * mm, "construction": true});
            skLineSegment(sketch, "E338", {"start": v(609.6, 403.23) * mm, "end": v(812.8, 403.23) * mm, "construction": true});
            skLineSegment(sketch, "E339", {"start": v(0, 593.73) * mm, "end": v(203.2, 593.73) * mm, "construction": true});
            skLineSegment(sketch, "E340", {"start": v(203.2, 593.73) * mm, "end": v(406.4, 593.73) * mm, "construction": true});
            skLineSegment(sketch, "E341", {"start": v(406.4, 593.73) * mm, "end": v(609.6, 593.73) * mm, "construction": true});
            skLineSegment(sketch, "E342", {"start": v(609.6, 593.73) * mm, "end": v(812.8, 593.73) * mm, "construction": true});
            skCircle(sketch, "E343", {"center": v(812.8, 0) * mm, "radius": 14.29 * mm});
            skCircle(sketch, "E344", {"center": v(812.8, 0) * mm, "radius": 11.11 * mm});
            skCircle(sketch, "E345", {"center": v(812.8, 0) * mm, "radius": 10.32 * mm});
            skCircle(sketch, "E346", {"center": v(812.8, 0) * mm, "radius": 25.4 * mm});
            skCircle(sketch, "E347", {"center": v(406.4, 0) * mm, "radius": 14.29 * mm});
            skCircle(sketch, "E348", {"center": v(406.4, 0) * mm, "radius": 11.11 * mm});
            skCircle(sketch, "E349", {"center": v(406.4, 0) * mm, "radius": 10.32 * mm});
            skCircle(sketch, "E350", {"center": v(406.4, 0) * mm, "radius": 25.4 * mm});
            skCircle(sketch, "E351", {"center": v(203.2, 254) * mm, "radius": 14.29 * mm});
            skCircle(sketch, "E352", {"center": v(203.2, 254) * mm, "radius": 11.11 * mm});
            skCircle(sketch, "E353", {"center": v(203.2, 254) * mm, "radius": 10.32 * mm});
            skCircle(sketch, "E354", {"center": v(203.2, 254) * mm, "radius": 25.4 * mm});
            skCircle(sketch, "E355", {"center": v(203.2, 593.73) * mm, "radius": 14.29 * mm});
            skCircle(sketch, "E356", {"center": v(203.2, 593.73) * mm, "radius": 11.11 * mm});
            skCircle(sketch, "E357", {"center": v(203.2, 593.73) * mm, "radius": 10.32 * mm});
            skCircle(sketch, "E358", {"center": v(203.2, 593.73) * mm, "radius": 25.4 * mm});
            skCircle(sketch, "E359", {"center": v(812.8, 254) * mm, "radius": 14.29 * mm});
            skCircle(sketch, "E360", {"center": v(812.8, 254) * mm, "radius": 11.11 * mm});
            skCircle(sketch, "E361", {"center": v(812.8, 254) * mm, "radius": 10.32 * mm});
            skCircle(sketch, "E362", {"center": v(812.8, 254) * mm, "radius": 25.4 * mm});
            skCircle(sketch, "E363", {"center": v(609.6, 0) * mm, "radius": 14.29 * mm});
            skCircle(sketch, "E364", {"center": v(609.6, 0) * mm, "radius": 11.11 * mm});
            skCircle(sketch, "E365", {"center": v(609.6, 0) * mm, "radius": 10.32 * mm});
            skCircle(sketch, "E366", {"center": v(609.6, 0) * mm, "radius": 25.4 * mm});
            skCircle(sketch, "E367", {"center": v(609.6, 593.73) * mm, "radius": 14.29 * mm});
            skCircle(sketch, "E368", {"center": v(609.6, 593.73) * mm, "radius": 11.11 * mm});
            skCircle(sketch, "E369", {"center": v(609.6, 593.73) * mm, "radius": 10.32 * mm});
            skCircle(sketch, "E370", {"center": v(609.6, 593.73) * mm, "radius": 25.4 * mm});
            skCircle(sketch, "E371", {"center": v(406.4, 254) * mm, "radius": 14.29 * mm});
            skCircle(sketch, "E372", {"center": v(406.4, 254) * mm, "radius": 11.11 * mm});
            skCircle(sketch, "E373", {"center": v(406.4, 254) * mm, "radius": 10.32 * mm});
            skCircle(sketch, "E374", {"center": v(406.4, 254) * mm, "radius": 25.4 * mm});
            skCircle(sketch, "E375", {"center": v(406.4, 593.73) * mm, "radius": 14.29 * mm});
            skCircle(sketch, "E376", {"center": v(406.4, 593.73) * mm, "radius": 11.11 * mm});
            skCircle(sketch, "E377", {"center": v(406.4, 593.73) * mm, "radius": 10.32 * mm});
            skCircle(sketch, "E378", {"center": v(406.4, 593.73) * mm, "radius": 25.4 * mm});
            skCircle(sketch, "E379", {"center": v(609.6, 254) * mm, "radius": 14.29 * mm});
            skCircle(sketch, "E380", {"center": v(609.6, 254) * mm, "radius": 11.11 * mm});
            skCircle(sketch, "E381", {"center": v(609.6, 254) * mm, "radius": 10.32 * mm});
            skCircle(sketch, "E382", {"center": v(609.6, 254) * mm, "radius": 25.4 * mm});
            skCircle(sketch, "E383", {"center": v(203.2, 0) * mm, "radius": 14.29 * mm});
            skCircle(sketch, "E384", {"center": v(203.2, 0) * mm, "radius": 11.11 * mm});
            skCircle(sketch, "E385", {"center": v(203.2, 0) * mm, "radius": 10.32 * mm});
            skCircle(sketch, "E386", {"center": v(203.2, 0) * mm, "radius": 25.4 * mm});
            skCircle(sketch, "E387", {"center": v(0, 254) * mm, "radius": 14.29 * mm});
            skCircle(sketch, "E388", {"center": v(0, 254) * mm, "radius": 11.11 * mm});
            skCircle(sketch, "E389", {"center": v(0, 254) * mm, "radius": 10.32 * mm});
            skCircle(sketch, "E390", {"center": v(0, 254) * mm, "radius": 25.4 * mm});
            skCircle(sketch, "E391", {"center": v(0, 0) * mm, "radius": 14.29 * mm});
            skCircle(sketch, "E392", {"center": v(0, 0) * mm, "radius": 11.11 * mm});
            skCircle(sketch, "E393", {"center": v(0, 0) * mm, "radius": 10.32 * mm});
            skCircle(sketch, "E394", {"center": v(0, 0) * mm, "radius": 25.4 * mm});
            skSolve(sketch);
        }
        {
            var Q0;
            Q0=qCreatedBy(makeId("Top.planeOp"),FACE);
            cPlane(context, id + "F28", {"entities" : qUnion([Q0]), "cplaneType" : CPlaneType.OFFSET, "offset" : 76.2 * mm, "width" : 152.4 * mm, "height" : 152.4 * mm});
        }
        {
            var Q0;
            Q0=qCreatedBy(id+"F28.planeOp",FACE);
            var sketch = newSketch(context, id + "F29", { "sketchPlane" : qUnion([Q0])});
            skLineSegment(sketch, "E395", {"start": v(0, 0) * mm, "end": v(0, 254) * mm, "construction": true});
            skLineSegment(sketch, "E396", {"start": v(0, 254) * mm, "end": v(0, 403.22) * mm, "construction": true});
            skLineSegment(sketch, "E397", {"start": v(203.2, 0) * mm, "end": v(203.2, 254) * mm, "construction": true});
            skLineSegment(sketch, "E398", {"start": v(203.2, 254) * mm, "end": v(203.2, 403.22) * mm, "construction": true});
            skLineSegment(sketch, "E399", {"start": v(203.2, 403.22) * mm, "end": v(203.2, 593.73) * mm, "construction": true});
            skLineSegment(sketch, "E400", {"start": v(406.4, 0) * mm, "end": v(406.4, 254) * mm, "construction": true});
            skLineSegment(sketch, "E401", {"start": v(406.4, 254) * mm, "end": v(406.4, 593.73) * mm, "construction": true});
            skLineSegment(sketch, "E402", {"start": v(609.6, 0) * mm, "end": v(609.6, 254) * mm, "construction": true});
            skLineSegment(sketch, "E403", {"start": v(609.6, 254) * mm, "end": v(609.6, 403.23) * mm, "construction": true});
            skLineSegment(sketch, "E404", {"start": v(609.6, 403.23) * mm, "end": v(609.6, 593.73) * mm, "construction": true});
            skLineSegment(sketch, "E405", {"start": v(812.8, 0) * mm, "end": v(812.8, 254) * mm, "construction": true});
            skLineSegment(sketch, "E406", {"start": v(812.8, 254) * mm, "end": v(812.8, 403.23) * mm, "construction": true});
            skCircle(sketch, "E407", {"center": v(609.6, 254) * mm, "radius": 14.29 * mm});
            skCircle(sketch, "E408", {"center": v(609.6, 254) * mm, "radius": 11.11 * mm});
            skCircle(sketch, "E409", {"center": v(609.6, 254) * mm, "radius": 10.32 * mm});
            skCircle(sketch, "E410", {"center": v(609.6, 254) * mm, "radius": 25.4 * mm});
            skCircle(sketch, "E411", {"center": v(0, 403.23) * mm, "radius": 14.29 * mm});
            skCircle(sketch, "E412", {"center": v(0, 403.23) * mm, "radius": 11.11 * mm});
            skCircle(sketch, "E413", {"center": v(0, 403.23) * mm, "radius": 10.32 * mm});
            skCircle(sketch, "E414", {"center": v(0, 403.23) * mm, "radius": 25.4 * mm});
            skCircle(sketch, "E415", {"center": v(0, 0) * mm, "radius": 14.29 * mm});
            skCircle(sketch, "E416", {"center": v(0, 0) * mm, "radius": 11.11 * mm});
            skCircle(sketch, "E417", {"center": v(0, 0) * mm, "radius": 10.32 * mm});
            skCircle(sketch, "E418", {"center": v(0, 0) * mm, "radius": 25.4 * mm});
            skCircle(sketch, "E419", {"center": v(203.2, 254) * mm, "radius": 14.29 * mm});
            skCircle(sketch, "E420", {"center": v(203.2, 254) * mm, "radius": 11.11 * mm});
            skCircle(sketch, "E421", {"center": v(203.2, 254) * mm, "radius": 10.32 * mm});
            skCircle(sketch, "E422", {"center": v(203.2, 254) * mm, "radius": 25.4 * mm});
            skCircle(sketch, "E423", {"center": v(812.8, 403.23) * mm, "radius": 14.29 * mm});
            skCircle(sketch, "E424", {"center": v(812.8, 403.23) * mm, "radius": 11.11 * mm});
            skCircle(sketch, "E425", {"center": v(812.8, 403.23) * mm, "radius": 10.32 * mm});
            skCircle(sketch, "E426", {"center": v(812.8, 403.23) * mm, "radius": 25.4 * mm});
            skCircle(sketch, "E427", {"center": v(812.8, 254) * mm, "radius": 14.29 * mm});
            skCircle(sketch, "E428", {"center": v(812.8, 254) * mm, "radius": 11.11 * mm});
            skCircle(sketch, "E429", {"center": v(812.8, 254) * mm, "radius": 10.32 * mm});
            skCircle(sketch, "E430", {"center": v(812.8, 254) * mm, "radius": 25.4 * mm});
            skCircle(sketch, "E431", {"center": v(406.4, 0) * mm, "radius": 14.29 * mm});
            skCircle(sketch, "E432", {"center": v(406.4, 0) * mm, "radius": 11.11 * mm});
            skCircle(sketch, "E433", {"center": v(406.4, 0) * mm, "radius": 10.32 * mm});
            skCircle(sketch, "E434", {"center": v(406.4, 0) * mm, "radius": 25.4 * mm});
            skCircle(sketch, "E435", {"center": v(0, 254) * mm, "radius": 14.29 * mm});
            skCircle(sketch, "E436", {"center": v(0, 254) * mm, "radius": 11.11 * mm});
            skCircle(sketch, "E437", {"center": v(0, 254) * mm, "radius": 10.32 * mm});
            skCircle(sketch, "E438", {"center": v(0, 254) * mm, "radius": 25.4 * mm});
            skCircle(sketch, "E439", {"center": v(609.6, 403.23) * mm, "radius": 14.29 * mm});
            skCircle(sketch, "E440", {"center": v(609.6, 403.23) * mm, "radius": 11.11 * mm});
            skCircle(sketch, "E441", {"center": v(609.6, 403.23) * mm, "radius": 10.32 * mm});
            skCircle(sketch, "E442", {"center": v(609.6, 403.23) * mm, "radius": 25.4 * mm});
            skCircle(sketch, "E443", {"center": v(203.2, 0) * mm, "radius": 14.29 * mm});
            skCircle(sketch, "E444", {"center": v(203.2, 0) * mm, "radius": 11.11 * mm});
            skCircle(sketch, "E445", {"center": v(203.2, 0) * mm, "radius": 10.32 * mm});
            skCircle(sketch, "E446", {"center": v(203.2, 0) * mm, "radius": 25.4 * mm});
            skCircle(sketch, "E447", {"center": v(203.2, 403.22) * mm, "radius": 14.29 * mm});
            skCircle(sketch, "E448", {"center": v(203.2, 403.22) * mm, "radius": 11.11 * mm});
            skCircle(sketch, "E449", {"center": v(203.2, 403.22) * mm, "radius": 10.32 * mm});
            skCircle(sketch, "E450", {"center": v(203.2, 403.22) * mm, "radius": 25.4 * mm});
            skCircle(sketch, "E451", {"center": v(203.2, 593.73) * mm, "radius": 14.29 * mm});
            skCircle(sketch, "E452", {"center": v(203.2, 593.73) * mm, "radius": 11.11 * mm});
            skCircle(sketch, "E453", {"center": v(203.2, 593.73) * mm, "radius": 10.32 * mm});
            skCircle(sketch, "E454", {"center": v(203.2, 593.73) * mm, "radius": 25.4 * mm});
            skCircle(sketch, "E455", {"center": v(609.6, 593.73) * mm, "radius": 14.29 * mm});
            skCircle(sketch, "E456", {"center": v(609.6, 593.73) * mm, "radius": 11.11 * mm});
            skCircle(sketch, "E457", {"center": v(609.6, 593.73) * mm, "radius": 10.32 * mm});
            skCircle(sketch, "E458", {"center": v(609.6, 593.73) * mm, "radius": 25.4 * mm});
            skCircle(sketch, "E459", {"center": v(609.6, 0) * mm, "radius": 14.29 * mm});
            skCircle(sketch, "E460", {"center": v(609.6, 0) * mm, "radius": 11.11 * mm});
            skCircle(sketch, "E461", {"center": v(609.6, 0) * mm, "radius": 10.32 * mm});
            skCircle(sketch, "E462", {"center": v(609.6, 0) * mm, "radius": 25.4 * mm});
            skCircle(sketch, "E463", {"center": v(406.4, 254) * mm, "radius": 14.29 * mm});
            skCircle(sketch, "E464", {"center": v(406.4, 254) * mm, "radius": 11.11 * mm});
            skCircle(sketch, "E465", {"center": v(406.4, 254) * mm, "radius": 10.32 * mm});
            skCircle(sketch, "E466", {"center": v(406.4, 254) * mm, "radius": 25.4 * mm});
            skCircle(sketch, "E467", {"center": v(406.4, 593.73) * mm, "radius": 14.29 * mm});
            skCircle(sketch, "E468", {"center": v(406.4, 593.73) * mm, "radius": 11.11 * mm});
            skCircle(sketch, "E469", {"center": v(406.4, 593.73) * mm, "radius": 10.32 * mm});
            skCircle(sketch, "E470", {"center": v(406.4, 593.73) * mm, "radius": 25.4 * mm});
            skCircle(sketch, "E471", {"center": v(812.8, 0) * mm, "radius": 14.29 * mm});
            skCircle(sketch, "E472", {"center": v(812.8, 0) * mm, "radius": 11.11 * mm});
            skCircle(sketch, "E473", {"center": v(812.8, 0) * mm, "radius": 10.32 * mm});
            skCircle(sketch, "E474", {"center": v(812.8, 0) * mm, "radius": 25.4 * mm});
            skSolve(sketch);
        }
        {
            var Q0;
            Q0=qCreatedBy(makeId("Top.planeOp"),FACE);
            cPlane(context, id + "F30", {"entities" : qUnion([Q0]), "cplaneType" : CPlaneType.OFFSET, "offset" : 228.6 * mm, "width" : 152.4 * mm, "height" : 152.4 * mm});
        }
        {
            var Q0;
            Q0=qCreatedBy(id+"F30.planeOp",FACE);
            var sketch = newSketch(context, id + "F31", { "sketchPlane" : qUnion([Q0])});
            skLineSegment(sketch, "E475", {"start": v(0, 403.23) * mm, "end": v(203.2, 403.23) * mm, "construction": true});
            skLineSegment(sketch, "E476", {"start": v(203.2, 593.73) * mm, "end": v(406.4, 593.73) * mm, "construction": true});
            skLineSegment(sketch, "E477", {"start": v(406.4, 593.73) * mm, "end": v(609.6, 593.73) * mm, "construction": true});
            skLineSegment(sketch, "E478", {"start": v(609.6, 403.23) * mm, "end": v(812.8, 403.23) * mm, "construction": true});
            skCircle(sketch, "E479", {"center": v(812.8, 403.23) * mm, "radius": 14.29 * mm});
            skCircle(sketch, "E480", {"center": v(812.8, 403.23) * mm, "radius": 11.11 * mm});
            skCircle(sketch, "E481", {"center": v(812.8, 403.23) * mm, "radius": 10.32 * mm});
            skCircle(sketch, "E482", {"center": v(812.8, 403.23) * mm, "radius": 25.4 * mm});
            skCircle(sketch, "E483", {"center": v(0, 403.23) * mm, "radius": 14.29 * mm});
            skCircle(sketch, "E484", {"center": v(0, 403.23) * mm, "radius": 11.11 * mm});
            skCircle(sketch, "E485", {"center": v(0, 403.23) * mm, "radius": 10.32 * mm});
            skCircle(sketch, "E486", {"center": v(0, 403.23) * mm, "radius": 25.4 * mm});
            skCircle(sketch, "E487", {"center": v(406.4, 593.73) * mm, "radius": 14.29 * mm});
            skCircle(sketch, "E488", {"center": v(406.4, 593.73) * mm, "radius": 11.11 * mm});
            skCircle(sketch, "E489", {"center": v(406.4, 593.73) * mm, "radius": 10.32 * mm});
            skCircle(sketch, "E490", {"center": v(406.4, 593.73) * mm, "radius": 25.4 * mm});
            skCircle(sketch, "E491", {"center": v(203.2, 403.23) * mm, "radius": 14.29 * mm});
            skCircle(sketch, "E492", {"center": v(203.2, 403.23) * mm, "radius": 11.11 * mm});
            skCircle(sketch, "E493", {"center": v(203.2, 403.23) * mm, "radius": 10.32 * mm});
            skCircle(sketch, "E494", {"center": v(203.2, 403.23) * mm, "radius": 25.4 * mm});
            skCircle(sketch, "E495", {"center": v(609.6, 593.73) * mm, "radius": 14.29 * mm});
            skCircle(sketch, "E496", {"center": v(609.6, 593.73) * mm, "radius": 11.11 * mm});
            skCircle(sketch, "E497", {"center": v(609.6, 593.73) * mm, "radius": 10.32 * mm});
            skCircle(sketch, "E498", {"center": v(609.6, 593.73) * mm, "radius": 25.4 * mm});
            skCircle(sketch, "E499", {"center": v(203.2, 593.73) * mm, "radius": 14.29 * mm});
            skCircle(sketch, "E500", {"center": v(203.2, 593.73) * mm, "radius": 11.11 * mm});
            skCircle(sketch, "E501", {"center": v(203.2, 593.73) * mm, "radius": 10.32 * mm});
            skCircle(sketch, "E502", {"center": v(203.2, 593.73) * mm, "radius": 25.4 * mm});
            skCircle(sketch, "E503", {"center": v(609.6, 403.23) * mm, "radius": 14.29 * mm});
            skCircle(sketch, "E504", {"center": v(609.6, 403.23) * mm, "radius": 11.11 * mm});
            skCircle(sketch, "E505", {"center": v(609.6, 403.23) * mm, "radius": 10.32 * mm});
            skCircle(sketch, "E506", {"center": v(609.6, 403.23) * mm, "radius": 25.4 * mm});
            skSolve(sketch);
        }
        {
            var Q0;
            Q0=qCreatedBy(makeId("Top.planeOp"),FACE);
            cPlane(context, id + "F32", {"entities" : qUnion([Q0]), "cplaneType" : CPlaneType.OFFSET, "offset" : 304.8 * mm, "width" : 152.4 * mm, "height" : 152.4 * mm});
        }
        {
            var Q0;
            Q0=qCreatedBy(id+"F32.planeOp",FACE);
            var sketch = newSketch(context, id + "F33", { "sketchPlane" : qUnion([Q0])});
            skLineSegment(sketch, "E507", {"start": v(0, 254) * mm, "end": v(0, 403.23) * mm, "construction": true});
            skLineSegment(sketch, "E508", {"start": v(203.2, 254) * mm, "end": v(203.2, 403.23) * mm, "construction": true});
            skLineSegment(sketch, "E509", {"start": v(203.2, 403.23) * mm, "end": v(203.2, 593.73) * mm, "construction": true});
            skLineSegment(sketch, "E510", {"start": v(406.4, 254) * mm, "end": v(406.4, 403.22) * mm, "construction": true});
            skLineSegment(sketch, "E511", {"start": v(406.4, 403.22) * mm, "end": v(406.4, 593.73) * mm, "construction": true});
            skLineSegment(sketch, "E512", {"start": v(609.6, 254) * mm, "end": v(609.6, 403.23) * mm, "construction": true});
            skLineSegment(sketch, "E513", {"start": v(609.6, 403.23) * mm, "end": v(609.6, 593.73) * mm, "construction": true});
            skLineSegment(sketch, "E514", {"start": v(812.8, 254) * mm, "end": v(812.8, 403.23) * mm, "construction": true});
            skCircle(sketch, "E515", {"center": v(609.6, 254) * mm, "radius": 14.29 * mm});
            skCircle(sketch, "E516", {"center": v(609.6, 254) * mm, "radius": 11.11 * mm});
            skCircle(sketch, "E517", {"center": v(609.6, 254) * mm, "radius": 10.32 * mm});
            skCircle(sketch, "E518", {"center": v(609.6, 254) * mm, "radius": 25.4 * mm});
            skCircle(sketch, "E519", {"center": v(406.4, 254) * mm, "radius": 14.29 * mm});
            skCircle(sketch, "E520", {"center": v(406.4, 254) * mm, "radius": 11.11 * mm});
            skCircle(sketch, "E521", {"center": v(406.4, 254) * mm, "radius": 10.32 * mm});
            skCircle(sketch, "E522", {"center": v(406.4, 254) * mm, "radius": 25.4 * mm});
            skCircle(sketch, "E523", {"center": v(203.2, 403.23) * mm, "radius": 14.29 * mm});
            skCircle(sketch, "E524", {"center": v(203.2, 403.23) * mm, "radius": 11.11 * mm});
            skCircle(sketch, "E525", {"center": v(203.2, 403.23) * mm, "radius": 10.32 * mm});
            skCircle(sketch, "E526", {"center": v(203.2, 403.23) * mm, "radius": 25.4 * mm});
            skCircle(sketch, "E527", {"center": v(406.4, 593.73) * mm, "radius": 14.29 * mm});
            skCircle(sketch, "E528", {"center": v(406.4, 593.73) * mm, "radius": 11.11 * mm});
            skCircle(sketch, "E529", {"center": v(406.4, 593.73) * mm, "radius": 10.32 * mm});
            skCircle(sketch, "E530", {"center": v(406.4, 593.73) * mm, "radius": 25.4 * mm});
            skCircle(sketch, "E531", {"center": v(812.8, 254) * mm, "radius": 14.29 * mm});
            skCircle(sketch, "E532", {"center": v(812.8, 254) * mm, "radius": 11.11 * mm});
            skCircle(sketch, "E533", {"center": v(812.8, 254) * mm, "radius": 10.32 * mm});
            skCircle(sketch, "E534", {"center": v(812.8, 254) * mm, "radius": 25.4 * mm});
            skCircle(sketch, "E535", {"center": v(609.6, 593.73) * mm, "radius": 14.29 * mm});
            skCircle(sketch, "E536", {"center": v(609.6, 593.73) * mm, "radius": 11.11 * mm});
            skCircle(sketch, "E537", {"center": v(609.6, 593.73) * mm, "radius": 10.32 * mm});
            skCircle(sketch, "E538", {"center": v(609.6, 593.73) * mm, "radius": 25.4 * mm});
            skCircle(sketch, "E539", {"center": v(812.8, 403.23) * mm, "radius": 14.29 * mm});
            skCircle(sketch, "E540", {"center": v(812.8, 403.23) * mm, "radius": 11.11 * mm});
            skCircle(sketch, "E541", {"center": v(812.8, 403.23) * mm, "radius": 10.32 * mm});
            skCircle(sketch, "E542", {"center": v(812.8, 403.23) * mm, "radius": 25.4 * mm});
            skCircle(sketch, "E543", {"center": v(0, 403.22) * mm, "radius": 14.29 * mm});
            skCircle(sketch, "E544", {"center": v(0, 403.22) * mm, "radius": 11.11 * mm});
            skCircle(sketch, "E545", {"center": v(0, 403.22) * mm, "radius": 10.32 * mm});
            skCircle(sketch, "E546", {"center": v(0, 403.22) * mm, "radius": 25.4 * mm});
            skCircle(sketch, "E547", {"center": v(203.2, 593.73) * mm, "radius": 14.29 * mm});
            skCircle(sketch, "E548", {"center": v(203.2, 593.73) * mm, "radius": 11.11 * mm});
            skCircle(sketch, "E549", {"center": v(203.2, 593.73) * mm, "radius": 10.32 * mm});
            skCircle(sketch, "E550", {"center": v(203.2, 593.73) * mm, "radius": 25.4 * mm});
            skCircle(sketch, "E551", {"center": v(609.6, 403.23) * mm, "radius": 14.29 * mm});
            skCircle(sketch, "E552", {"center": v(609.6, 403.23) * mm, "radius": 11.11 * mm});
            skCircle(sketch, "E553", {"center": v(609.6, 403.23) * mm, "radius": 10.32 * mm});
            skCircle(sketch, "E554", {"center": v(609.6, 403.23) * mm, "radius": 25.4 * mm});
            skCircle(sketch, "E555", {"center": v(203.2, 254) * mm, "radius": 14.29 * mm});
            skCircle(sketch, "E556", {"center": v(203.2, 254) * mm, "radius": 11.11 * mm});
            skCircle(sketch, "E557", {"center": v(203.2, 254) * mm, "radius": 10.32 * mm});
            skCircle(sketch, "E558", {"center": v(203.2, 254) * mm, "radius": 25.4 * mm});
            skCircle(sketch, "E559", {"center": v(0, 254) * mm, "radius": 14.29 * mm});
            skCircle(sketch, "E560", {"center": v(0, 254) * mm, "radius": 11.11 * mm});
            skCircle(sketch, "E561", {"center": v(0, 254) * mm, "radius": 10.32 * mm});
            skCircle(sketch, "E562", {"center": v(0, 254) * mm, "radius": 25.4 * mm});
            skPoint(sketch, "E563.center.orphan", {"position": v(406.4, 403.23) * mm});
            skSolve(sketch);
        }
        {
            var Q0;
            Q0=qCreatedBy(makeId("Top.planeOp"),FACE);
            cPlane(context, id + "F34", {"entities" : qUnion([Q0]), "cplaneType" : CPlaneType.OFFSET, "offset" : 381 * mm, "width" : 152.4 * mm, "height" : 152.4 * mm});
        }
        {
            var Q0;
            Q0=makeQuery(id+"F1.imprint","IMPRINT",FACE,{"disambiguationData":[TD([[makeQuery(id+"F1.imprint","IMPRINT",EDGE,{"derivedFrom":sQuery(id+"F1.wireOp",EDGE,"E63")}),1.0]])]});
            extrude(context, id + "F35", {"entities" : qUnion([Q0]), "depth" : 31.75 * mm, "offsetDistance" : 25.4 * mm});
        }
        {
            var Q0;
            Q0=makeQuery(id+"F1.imprint","IMPRINT",FACE,{"disambiguationData":[TD([[makeQuery(id+"F1.imprint","IMPRINT",EDGE,{"derivedFrom":sQuery(id+"F1.wireOp",EDGE,"E64")}),1.0]])]});
            extrude(context, id + "F36", {"entities" : qUnion([Q0]), "operationType" : NewBodyOperationType.ADD, "depth" : 14.29 * mm, "offsetDistance" : 25.4 * mm});
        }
        {
            var Q0;
            Q0=makeQuery(id+"F27.imprint","IMPRINT",FACE,{"disambiguationData":[TD([[makeQuery(id+"F27.imprint","IMPRINT",EDGE,{"derivedFrom":sQuery(id+"F27.wireOp",EDGE,"E391")}),1.0]])]});
            extrude(context, id + "F37", {"entities" : qUnion([Q0]), "operationType" : NewBodyOperationType.ADD, "endBound" : BoundingType.SYMMETRIC, "depth" : 63.5 * mm, "offsetDistance" : 25.4 * mm});
        }
        {
            var Q0;
            Q0=makeQuery(id+"F27.imprint","IMPRINT",FACE,{"disambiguationData":[TD([[makeQuery(id+"F27.imprint","IMPRINT",EDGE,{"derivedFrom":sQuery(id+"F27.wireOp",EDGE,"E392")}),1.0]])]});
            extrude(context, id + "F38", {"entities" : qUnion([Q0]), "operationType" : NewBodyOperationType.ADD, "endBound" : BoundingType.SYMMETRIC, "depth" : 28.57 * mm, "offsetDistance" : 25.4 * mm});
        }
        {
            var Q0;
            Q0=makeQuery(id+"F27.imprint","IMPRINT",FACE,{"disambiguationData":[TD([[makeQuery(id+"F27.imprint","IMPRINT",EDGE,{"derivedFrom":sQuery(id+"F27.wireOp",EDGE,"E393")}),1.0]])]});
            extrude(context, id + "F39", {"entities" : qUnion([Q0]), "operationType" : NewBodyOperationType.REMOVE, "endBound" : BoundingType.SYMMETRIC, "oppositeDirection" : true, "depth" : 28.57 * mm, "offsetDistance" : 25.4 * mm});
        }
        {
            var Q0;
            Q0=makeQuery(id+"F1.imprint","IMPRINT",FACE,{"disambiguationData":[TD([[makeQuery(id+"F1.imprint","IMPRINT",EDGE,{"derivedFrom":sQuery(id+"F1.wireOp",EDGE,"E65")}),1.0]])]});
            extrude(context, id + "F40", {"entities" : qUnion([Q0]), "operationType" : NewBodyOperationType.REMOVE, "depth" : 14.29 * mm, "offsetDistance" : 25.4 * mm});
        }
        {
            var Q0;
            Q0=makeQuery(id+"F1.imprint","IMPRINT",FACE,{"disambiguationData":[TD([[makeQuery(id+"F1.imprint","IMPRINT",EDGE,{"derivedFrom":sQuery(id+"F1.wireOp",EDGE,"E73.1.0.1")}),1.0]])]});
            extrude(context, id + "F41", {"entities" : qUnion([Q0]), "depth" : 14.29 * mm, "offsetDistance" : 25.4 * mm});
        }
        {
            var Q0;
            Q0=makeQuery(id+"F1.imprint","IMPRINT",FACE,{"disambiguationData":[TD([[makeQuery(id+"F1.imprint","IMPRINT",EDGE,{"derivedFrom":sQuery(id+"F1.wireOp",EDGE,"E73.1.0.1")}),-1.0]])]});
            extrude(context, id + "F42", {"entities" : qUnion([Q0]), "operationType" : NewBodyOperationType.ADD, "depth" : 31.75 * mm, "offsetDistance" : 25.4 * mm});
        }
        {
            var Q0;
            Q0=makeQuery(id+"F27.imprint","IMPRINT",FACE,{"disambiguationData":[TD([[makeQuery(id+"F27.imprint","IMPRINT",EDGE,{"derivedFrom":sQuery(id+"F27.wireOp",EDGE,"E388")}),1.0]])]});
            extrude(context, id + "F43", {"entities" : qUnion([Q0]), "operationType" : NewBodyOperationType.ADD, "endBound" : BoundingType.SYMMETRIC, "depth" : 28.57 * mm, "offsetDistance" : 25.4 * mm});
        }
        {
            var Q0;
            Q0=makeQuery(id+"F27.imprint","IMPRINT",FACE,{"disambiguationData":[TD([[makeQuery(id+"F27.imprint","IMPRINT",EDGE,{"derivedFrom":sQuery(id+"F27.wireOp",EDGE,"E387")}),1.0]])]});
            extrude(context, id + "F44", {"entities" : qUnion([Q0]), "operationType" : NewBodyOperationType.ADD, "endBound" : BoundingType.SYMMETRIC, "depth" : 63.5 * mm, "offsetDistance" : 25.4 * mm});
        }
        {
            var Q0;
            Q0=makeQuery(id+"F27.imprint","IMPRINT",FACE,{"disambiguationData":[TD([[makeQuery(id+"F27.imprint","IMPRINT",EDGE,{"derivedFrom":sQuery(id+"F27.wireOp",EDGE,"E389")}),1.0]])]});
            extrude(context, id + "F45", {"entities" : qUnion([Q0]), "operationType" : NewBodyOperationType.REMOVE, "endBound" : BoundingType.SYMMETRIC, "oppositeDirection" : true, "depth" : 28.57 * mm, "offsetDistance" : 25.4 * mm});
        }
        {
            var Q0;
            Q0=makeQuery(id+"F1.imprint","IMPRINT",FACE,{"disambiguationData":[TD([[makeQuery(id+"F1.imprint","IMPRINT",EDGE,{"derivedFrom":sQuery(id+"F1.wireOp",EDGE,"E73.1.0.2")}),1.0]])]});
            extrude(context, id + "F46", {"entities" : qUnion([Q0]), "operationType" : NewBodyOperationType.REMOVE, "depth" : 14.29 * mm, "offsetDistance" : 25.4 * mm});
        }
        {
            var Q0;
            Q0=makeQuery(id+"F1.imprint","IMPRINT",FACE,{"disambiguationData":[TD([[makeQuery(id+"F1.imprint","IMPRINT",EDGE,{"derivedFrom":sQuery(id+"F1.wireOp",EDGE,"E69")}),1.0]])]});
            extrude(context, id + "F47", {"entities" : qUnion([Q0]), "depth" : 14.29 * mm, "offsetDistance" : 25.4 * mm});
        }
        {
            var Q0;
            Q0=makeQuery(id+"F1.imprint","IMPRINT",FACE,{"disambiguationData":[TD([[makeQuery(id+"F1.imprint","IMPRINT",EDGE,{"derivedFrom":sQuery(id+"F1.wireOp",EDGE,"E68")}),1.0]])]});
            extrude(context, id + "F48", {"entities" : qUnion([Q0]), "operationType" : NewBodyOperationType.ADD, "depth" : 31.75 * mm, "offsetDistance" : 25.4 * mm});
        }
        {
            var Q0;
            Q0=makeQuery(id+"F31.imprint","IMPRINT",FACE,{"disambiguationData":[TD([[makeQuery(id+"F31.imprint","IMPRINT",EDGE,{"derivedFrom":sQuery(id+"F31.wireOp",EDGE,"E485")}),1.0]])]});
            extrude(context, id + "F49", {"entities" : qUnion([Q0]), "operationType" : NewBodyOperationType.REMOVE, "endBound" : BoundingType.SYMMETRIC, "oppositeDirection" : true, "depth" : 28.57 * mm, "offsetDistance" : 25.4 * mm});
        }
        {
            var Q0;
            Q0=makeQuery(id+"F31.imprint","IMPRINT",FACE,{"disambiguationData":[TD([[makeQuery(id+"F31.imprint","IMPRINT",EDGE,{"derivedFrom":sQuery(id+"F31.wireOp",EDGE,"E484")}),1.0]])]});
            extrude(context, id + "F50", {"entities" : qUnion([Q0]), "operationType" : NewBodyOperationType.ADD, "endBound" : BoundingType.SYMMETRIC, "depth" : 28.57 * mm, "offsetDistance" : 25.4 * mm});
        }
        {
            var Q0;
            Q0=makeQuery(id+"F31.imprint","IMPRINT",FACE,{"disambiguationData":[TD([[makeQuery(id+"F31.imprint","IMPRINT",EDGE,{"derivedFrom":sQuery(id+"F31.wireOp",EDGE,"E483")}),1.0]])]});
            extrude(context, id + "F51", {"entities" : qUnion([Q0]), "operationType" : NewBodyOperationType.ADD, "endBound" : BoundingType.SYMMETRIC, "depth" : 63.5 * mm, "offsetDistance" : 25.4 * mm});
        }
        {
            var Q0;
            Q0=makeQuery(id+"F1.imprint","IMPRINT",FACE,{"disambiguationData":[TD([[makeQuery(id+"F1.imprint","IMPRINT",EDGE,{"derivedFrom":sQuery(id+"F1.wireOp",EDGE,"E70")}),1.0]])]});
            extrude(context, id + "F52", {"entities" : qUnion([Q0]), "operationType" : NewBodyOperationType.REMOVE, "depth" : 14.29 * mm, "offsetDistance" : 25.4 * mm});
        }
        {
            var Q0;
            Q0=makeQuery(id+"F0.imprint","IMPRINT",FACE,{"disambiguationData":[TD([[makeQuery(id+"F0.imprint","IMPRINT",EDGE,{"derivedFrom":sQuery(id+"F0.wireOp",EDGE,"E33")}),1.0]])]});
            extrude(context, id + "F53", {"entities" : qUnion([Q0]), "oppositeDirection" : true, "depth" : 14.29 * mm, "offsetDistance" : 25.4 * mm});
        }
        {
            var Q0;
            Q0=makeQuery(id+"F0.imprint","IMPRINT",FACE,{"disambiguationData":[TD([[makeQuery(id+"F0.imprint","IMPRINT",EDGE,{"derivedFrom":sQuery(id+"F0.wireOp",EDGE,"E32")}),1.0]])]});
            extrude(context, id + "F54", {"entities" : qUnion([Q0]), "operationType" : NewBodyOperationType.ADD, "oppositeDirection" : true, "depth" : 31.75 * mm, "offsetDistance" : 25.4 * mm});
        }
        {
            var Q0;
            Q0=makeQuery(id+"F29.imprint","IMPRINT",FACE,{"disambiguationData":[TD([[makeQuery(id+"F29.imprint","IMPRINT",EDGE,{"derivedFrom":sQuery(id+"F29.wireOp",EDGE,"E417")}),1.0]])]});
            extrude(context, id + "F55", {"entities" : qUnion([Q0]), "operationType" : NewBodyOperationType.REMOVE, "endBound" : BoundingType.SYMMETRIC, "oppositeDirection" : true, "depth" : 28.57 * mm, "offsetDistance" : 25.4 * mm});
        }
        {
            var Q0;
            Q0=makeQuery(id+"F29.imprint","IMPRINT",FACE,{"disambiguationData":[TD([[makeQuery(id+"F29.imprint","IMPRINT",EDGE,{"derivedFrom":sQuery(id+"F29.wireOp",EDGE,"E416")}),1.0]])]});
            extrude(context, id + "F56", {"entities" : qUnion([Q0]), "operationType" : NewBodyOperationType.ADD, "endBound" : BoundingType.SYMMETRIC, "depth" : 28.57 * mm, "offsetDistance" : 25.4 * mm});
        }
        {
            var Q0;
            Q0=makeQuery(id+"F29.imprint","IMPRINT",FACE,{"disambiguationData":[TD([[makeQuery(id+"F29.imprint","IMPRINT",EDGE,{"derivedFrom":sQuery(id+"F29.wireOp",EDGE,"E415")}),1.0]])]});
            extrude(context, id + "F57", {"entities" : qUnion([Q0]), "operationType" : NewBodyOperationType.ADD, "endBound" : BoundingType.SYMMETRIC, "depth" : 63.5 * mm, "offsetDistance" : 25.4 * mm});
        }
        {
            var Q0;
            Q0=makeQuery(id+"F0.imprint","IMPRINT",FACE,{"disambiguationData":[TD([[makeQuery(id+"F0.imprint","IMPRINT",EDGE,{"derivedFrom":sQuery(id+"F0.wireOp",EDGE,"E34")}),1.0]])]});
            extrude(context, id + "F58", {"entities" : qUnion([Q0]), "operationType" : NewBodyOperationType.REMOVE, "oppositeDirection" : true, "depth" : 14.29 * mm, "offsetDistance" : 25.4 * mm});
        }
        {
            var Q0;
            Q0=makeQuery(id+"F27.imprint","IMPRINT",FACE,{"disambiguationData":[TD([[makeQuery(id+"F27.imprint","IMPRINT",EDGE,{"derivedFrom":sQuery(id+"F27.wireOp",EDGE,"E384")}),1.0]])]});
            extrude(context, id + "F59", {"entities" : qUnion([Q0]), "depth" : 14.29 * mm, "offsetDistance" : 25.4 * mm});
        }
        {
            var Q0;
            Q0=makeQuery(id+"F27.imprint","IMPRINT",FACE,{"disambiguationData":[TD([[makeQuery(id+"F27.imprint","IMPRINT",EDGE,{"derivedFrom":sQuery(id+"F27.wireOp",EDGE,"E383")}),1.0]])]});
            extrude(context, id + "F60", {"entities" : qUnion([Q0]), "operationType" : NewBodyOperationType.ADD, "depth" : 31.75 * mm, "offsetDistance" : 25.4 * mm});
        }
        {
            var Q0;
            Q0=makeQuery(id+"F15.imprint","IMPRINT",FACE,{"disambiguationData":[TD([[makeQuery(id+"F15.imprint","IMPRINT",EDGE,{"derivedFrom":sQuery(id+"F15.wireOp",EDGE,"E96")}),1.0]])]});
            extrude(context, id + "F61", {"entities" : qUnion([Q0]), "operationType" : NewBodyOperationType.REMOVE, "endBound" : BoundingType.SYMMETRIC, "depth" : 28.57 * mm, "offsetDistance" : 25.4 * mm});
        }
        {
            var Q0;
            Q0=makeQuery(id+"F15.imprint","IMPRINT",FACE,{"disambiguationData":[TD([[makeQuery(id+"F15.imprint","IMPRINT",EDGE,{"derivedFrom":sQuery(id+"F15.wireOp",EDGE,"E95")}),1.0]])]});
            extrude(context, id + "F62", {"entities" : qUnion([Q0]), "operationType" : NewBodyOperationType.ADD, "endBound" : BoundingType.SYMMETRIC, "depth" : 28.57 * mm, "offsetDistance" : 25.4 * mm});
        }
        {
            var Q0;
            Q0=makeQuery(id+"F15.imprint","IMPRINT",FACE,{"disambiguationData":[TD([[makeQuery(id+"F15.imprint","IMPRINT",EDGE,{"derivedFrom":sQuery(id+"F15.wireOp",EDGE,"E94")}),1.0]])]});
            extrude(context, id + "F63", {"entities" : qUnion([Q0]), "operationType" : NewBodyOperationType.ADD, "endBound" : BoundingType.SYMMETRIC, "depth" : 63.5 * mm, "offsetDistance" : 25.4 * mm});
        }
        {
            var Q0;
            Q0=makeQuery(id+"F27.imprint","IMPRINT",FACE,{"disambiguationData":[TD([[makeQuery(id+"F27.imprint","IMPRINT",EDGE,{"derivedFrom":sQuery(id+"F27.wireOp",EDGE,"E385")}),1.0]])]});
            extrude(context, id + "F64", {"entities" : qUnion([Q0]), "operationType" : NewBodyOperationType.REMOVE, "depth" : 25.4 * mm, "offsetDistance" : 25.4 * mm});
        }
        {
            var Q0;
            Q0=makeQuery(id+"F0.imprint","IMPRINT",FACE,{"disambiguationData":[TD([[makeQuery(id+"F0.imprint","IMPRINT",EDGE,{"derivedFrom":sQuery(id+"F0.wireOp",EDGE,"E53")}),1.0]])]});
            extrude(context, id + "F65", {"entities" : qUnion([Q0]), "oppositeDirection" : true, "depth" : 14.29 * mm, "offsetDistance" : 25.4 * mm});
        }
        {
            var Q0;
            Q0=makeQuery(id+"F0.imprint","IMPRINT",FACE,{"disambiguationData":[TD([[makeQuery(id+"F0.imprint","IMPRINT",EDGE,{"derivedFrom":sQuery(id+"F0.wireOp",EDGE,"E52")}),1.0]])]});
            extrude(context, id + "F66", {"entities" : qUnion([Q0]), "operationType" : NewBodyOperationType.ADD, "oppositeDirection" : true, "depth" : 31.75 * mm, "offsetDistance" : 25.4 * mm});
        }
        {
            var Q0;
            Q0=makeQuery(id+"F29.imprint","IMPRINT",FACE,{"disambiguationData":[TD([[makeQuery(id+"F29.imprint","IMPRINT",EDGE,{"derivedFrom":sQuery(id+"F29.wireOp",EDGE,"E445")}),1.0]])]});
            extrude(context, id + "F67", {"entities" : qUnion([Q0]), "operationType" : NewBodyOperationType.REMOVE, "endBound" : BoundingType.SYMMETRIC, "oppositeDirection" : true, "depth" : 28.57 * mm, "offsetDistance" : 25.4 * mm});
        }
        {
            var Q0;
            Q0=makeQuery(id+"F29.imprint","IMPRINT",FACE,{"disambiguationData":[TD([[makeQuery(id+"F29.imprint","IMPRINT",EDGE,{"derivedFrom":sQuery(id+"F29.wireOp",EDGE,"E444")}),1.0]])]});
            extrude(context, id + "F68", {"entities" : qUnion([Q0]), "operationType" : NewBodyOperationType.ADD, "endBound" : BoundingType.SYMMETRIC, "depth" : 28.57 * mm, "offsetDistance" : 25.4 * mm});
        }
        {
            var Q0;
            Q0=makeQuery(id+"F29.imprint","IMPRINT",FACE,{"disambiguationData":[TD([[makeQuery(id+"F29.imprint","IMPRINT",EDGE,{"derivedFrom":sQuery(id+"F29.wireOp",EDGE,"E443")}),1.0]])]});
            extrude(context, id + "F69", {"entities" : qUnion([Q0]), "operationType" : NewBodyOperationType.ADD, "endBound" : BoundingType.SYMMETRIC, "depth" : 63.5 * mm, "offsetDistance" : 25.4 * mm});
        }
        {
            var Q0;
            Q0=makeQuery(id+"F0.imprint","IMPRINT",FACE,{"disambiguationData":[TD([[makeQuery(id+"F0.imprint","IMPRINT",EDGE,{"derivedFrom":sQuery(id+"F0.wireOp",EDGE,"E54")}),1.0]])]});
            extrude(context, id + "F70", {"entities" : qUnion([Q0]), "operationType" : NewBodyOperationType.REMOVE, "oppositeDirection" : true, "depth" : 14.29 * mm, "offsetDistance" : 25.4 * mm});
        }
        {
            var Q0;
            Q0=makeQuery(id+"F0.imprint","IMPRINT",FACE,{"disambiguationData":[TD([[makeQuery(id+"F0.imprint","IMPRINT",EDGE,{"derivedFrom":sQuery(id+"F0.wireOp",EDGE,"E29")}),1.0]])]});
            extrude(context, id + "F71", {"entities" : qUnion([Q0]), "oppositeDirection" : true, "depth" : 14.29 * mm, "offsetDistance" : 25.4 * mm});
        }
        {
            var Q0;
            Q0=makeQuery(id+"F0.imprint","IMPRINT",FACE,{"disambiguationData":[TD([[makeQuery(id+"F0.imprint","IMPRINT",EDGE,{"derivedFrom":sQuery(id+"F0.wireOp",EDGE,"E28")}),1.0]])]});
            extrude(context, id + "F72", {"entities" : qUnion([Q0]), "operationType" : NewBodyOperationType.ADD, "oppositeDirection" : true, "depth" : 25.4 * mm, "offsetDistance" : 25.4 * mm});
        }
        {
            var Q0;
            Q0=makeQuery(id+"F29.imprint","IMPRINT",FACE,{"disambiguationData":[TD([[makeQuery(id+"F29.imprint","IMPRINT",EDGE,{"derivedFrom":sQuery(id+"F29.wireOp",EDGE,"E433")}),1.0]])]});
            extrude(context, id + "F73", {"entities" : qUnion([Q0]), "operationType" : NewBodyOperationType.REMOVE, "endBound" : BoundingType.SYMMETRIC, "oppositeDirection" : true, "depth" : 28.57 * mm, "offsetDistance" : 25.4 * mm});
        }
        {
            var Q0;
            Q0=makeQuery(id+"F29.imprint","IMPRINT",FACE,{"disambiguationData":[TD([[makeQuery(id+"F29.imprint","IMPRINT",EDGE,{"derivedFrom":sQuery(id+"F29.wireOp",EDGE,"E432")}),1.0]])]});
            extrude(context, id + "F74", {"entities" : qUnion([Q0]), "operationType" : NewBodyOperationType.ADD, "endBound" : BoundingType.SYMMETRIC, "depth" : 28.57 * mm, "offsetDistance" : 25.4 * mm});
        }
        {
            var Q0;
            Q0=makeQuery(id+"F29.imprint","IMPRINT",FACE,{"disambiguationData":[TD([[makeQuery(id+"F29.imprint","IMPRINT",EDGE,{"derivedFrom":sQuery(id+"F29.wireOp",EDGE,"E431")}),1.0]])]});
            extrude(context, id + "F75", {"entities" : qUnion([Q0]), "operationType" : NewBodyOperationType.ADD, "endBound" : BoundingType.SYMMETRIC, "depth" : 63.5 * mm, "offsetDistance" : 25.4 * mm});
        }
        {
            var Q0;
            Q0=makeQuery(id+"F0.imprint","IMPRINT",FACE,{"disambiguationData":[TD([[makeQuery(id+"F0.imprint","IMPRINT",EDGE,{"derivedFrom":sQuery(id+"F0.wireOp",EDGE,"E30")}),1.0]])]});
            extrude(context, id + "F76", {"entities" : qUnion([Q0]), "operationType" : NewBodyOperationType.REMOVE, "oppositeDirection" : true, "depth" : 14.29 * mm, "offsetDistance" : 25.4 * mm});
        }
        {
            var Q0;
            Q0=makeQuery(id+"F27.imprint","IMPRINT",FACE,{"disambiguationData":[TD([[makeQuery(id+"F27.imprint","IMPRINT",EDGE,{"derivedFrom":sQuery(id+"F27.wireOp",EDGE,"E364")}),1.0]])]});
            extrude(context, id + "F77", {"entities" : qUnion([Q0]), "depth" : 14.29 * mm, "offsetDistance" : 25.4 * mm});
        }
        {
            var Q0;
            Q0=makeQuery(id+"F27.imprint","IMPRINT",FACE,{"disambiguationData":[TD([[makeQuery(id+"F27.imprint","IMPRINT",EDGE,{"derivedFrom":sQuery(id+"F27.wireOp",EDGE,"E363")}),1.0]])]});
            extrude(context, id + "F78", {"entities" : qUnion([Q0]), "operationType" : NewBodyOperationType.ADD, "depth" : 31.75 * mm, "offsetDistance" : 25.4 * mm});
        }
        {
            var Q0;
            Q0=makeQuery(id+"F18.imprint","IMPRINT",FACE,{"disambiguationData":[TD([[makeQuery(id+"F18.imprint","IMPRINT",EDGE,{"derivedFrom":sQuery(id+"F18.wireOp",EDGE,"E143")}),1.0]])]});
            extrude(context, id + "F79", {"entities" : qUnion([Q0]), "operationType" : NewBodyOperationType.REMOVE, "endBound" : BoundingType.SYMMETRIC, "oppositeDirection" : true, "depth" : 28.57 * mm, "offsetDistance" : 25.4 * mm});
        }
        {
            var Q0;
            Q0=makeQuery(id+"F18.imprint","IMPRINT",FACE,{"disambiguationData":[TD([[makeQuery(id+"F18.imprint","IMPRINT",EDGE,{"derivedFrom":sQuery(id+"F18.wireOp",EDGE,"E142")}),1.0]])]});
            extrude(context, id + "F80", {"entities" : qUnion([Q0]), "operationType" : NewBodyOperationType.ADD, "endBound" : BoundingType.SYMMETRIC, "depth" : 28.57 * mm, "offsetDistance" : 25.4 * mm});
        }
        {
            var Q0;
            Q0=makeQuery(id+"F18.imprint","IMPRINT",FACE,{"disambiguationData":[TD([[makeQuery(id+"F18.imprint","IMPRINT",EDGE,{"derivedFrom":sQuery(id+"F18.wireOp",EDGE,"E141")}),1.0]])]});
            extrude(context, id + "F81", {"entities" : qUnion([Q0]), "operationType" : NewBodyOperationType.ADD, "endBound" : BoundingType.SYMMETRIC, "depth" : 63.5 * mm, "offsetDistance" : 25.4 * mm});
        }
        {
            var Q0;
            Q0=makeQuery(id+"F27.imprint","IMPRINT",FACE,{"disambiguationData":[TD([[makeQuery(id+"F27.imprint","IMPRINT",EDGE,{"derivedFrom":sQuery(id+"F27.wireOp",EDGE,"E365")}),1.0]])]});
            extrude(context, id + "F82", {"entities" : qUnion([Q0]), "operationType" : NewBodyOperationType.REMOVE, "depth" : 14.29 * mm, "offsetDistance" : 25.4 * mm});
        }
        {
            var Q0;
            Q0=makeQuery(id+"F20.imprint","IMPRINT",FACE,{"disambiguationData":[TD([[makeQuery(id+"F20.imprint","IMPRINT",EDGE,{"derivedFrom":sQuery(id+"F20.wireOp",EDGE,"E159")}),1.0]])]});
            extrude(context, id + "F83", {"entities" : qUnion([Q0]), "oppositeDirection" : true, "depth" : 14.29 * mm, "offsetDistance" : 25.4 * mm});
        }
        {
            var Q0;
            Q0=makeQuery(id+"F20.imprint","IMPRINT",FACE,{"disambiguationData":[TD([[makeQuery(id+"F20.imprint","IMPRINT",EDGE,{"derivedFrom":sQuery(id+"F20.wireOp",EDGE,"E158")}),1.0]])]});
            extrude(context, id + "F84", {"entities" : qUnion([Q0]), "operationType" : NewBodyOperationType.ADD, "oppositeDirection" : true, "depth" : 31.75 * mm, "offsetDistance" : 25.4 * mm});
        }
        {
            var Q0;
            Q0=makeQuery(id+"F27.imprint","IMPRINT",FACE,{"disambiguationData":[TD([[makeQuery(id+"F27.imprint","IMPRINT",EDGE,{"derivedFrom":sQuery(id+"F27.wireOp",EDGE,"E345")}),1.0]])]});
            extrude(context, id + "F85", {"entities" : qUnion([Q0]), "operationType" : NewBodyOperationType.REMOVE, "endBound" : BoundingType.SYMMETRIC, "oppositeDirection" : true, "depth" : 28.57 * mm, "offsetDistance" : 25.4 * mm});
        }
        {
            var Q0;
            Q0=makeQuery(id+"F27.imprint","IMPRINT",FACE,{"disambiguationData":[TD([[makeQuery(id+"F27.imprint","IMPRINT",EDGE,{"derivedFrom":sQuery(id+"F27.wireOp",EDGE,"E344")}),1.0]])]});
            extrude(context, id + "F86", {"entities" : qUnion([Q0]), "operationType" : NewBodyOperationType.ADD, "endBound" : BoundingType.SYMMETRIC, "depth" : 28.57 * mm, "offsetDistance" : 25.4 * mm});
        }
        {
            var Q0;
            Q0=makeQuery(id+"F27.imprint","IMPRINT",FACE,{"disambiguationData":[TD([[makeQuery(id+"F27.imprint","IMPRINT",EDGE,{"derivedFrom":sQuery(id+"F27.wireOp",EDGE,"E343")}),1.0]])]});
            extrude(context, id + "F87", {"entities" : qUnion([Q0]), "operationType" : NewBodyOperationType.ADD, "endBound" : BoundingType.SYMMETRIC, "depth" : 63.5 * mm, "offsetDistance" : 25.4 * mm});
        }
        {
            var Q0;
            Q0=makeQuery(id+"F20.imprint","IMPRINT",FACE,{"disambiguationData":[TD([[makeQuery(id+"F20.imprint","IMPRINT",EDGE,{"derivedFrom":sQuery(id+"F20.wireOp",EDGE,"E160")}),1.0]])]});
            extrude(context, id + "F88", {"entities" : qUnion([Q0]), "operationType" : NewBodyOperationType.REMOVE, "oppositeDirection" : true, "depth" : 14.29 * mm, "offsetDistance" : 25.4 * mm});
        }
        {
            var Q0;
            Q0=makeQuery(id+"F0.imprint","IMPRINT",FACE,{"disambiguationData":[TD([[makeQuery(id+"F0.imprint","IMPRINT",EDGE,{"derivedFrom":sQuery(id+"F0.wireOp",EDGE,"E41")}),1.0]])]});
            extrude(context, id + "F89", {"entities" : qUnion([Q0]), "oppositeDirection" : true, "depth" : 14.29 * mm, "offsetDistance" : 25.4 * mm});
        }
        {
            var Q0;
            Q0=makeQuery(id+"F0.imprint","IMPRINT",FACE,{"disambiguationData":[TD([[makeQuery(id+"F0.imprint","IMPRINT",EDGE,{"derivedFrom":sQuery(id+"F0.wireOp",EDGE,"E40")}),1.0]])]});
            extrude(context, id + "F90", {"entities" : qUnion([Q0]), "operationType" : NewBodyOperationType.ADD, "oppositeDirection" : true, "depth" : 31.75 * mm, "offsetDistance" : 25.4 * mm});
        }
        {
            var Q0;
            Q0=makeQuery(id+"F29.imprint","IMPRINT",FACE,{"disambiguationData":[TD([[makeQuery(id+"F29.imprint","IMPRINT",EDGE,{"derivedFrom":sQuery(id+"F29.wireOp",EDGE,"E473")}),1.0]])]});
            extrude(context, id + "F91", {"entities" : qUnion([Q0]), "operationType" : NewBodyOperationType.REMOVE, "endBound" : BoundingType.SYMMETRIC, "oppositeDirection" : true, "depth" : 28.57 * mm, "offsetDistance" : 25.4 * mm});
        }
        {
            var Q0;
            Q0=makeQuery(id+"F29.imprint","IMPRINT",FACE,{"disambiguationData":[TD([[makeQuery(id+"F29.imprint","IMPRINT",EDGE,{"derivedFrom":sQuery(id+"F29.wireOp",EDGE,"E472")}),1.0]])]});
            extrude(context, id + "F92", {"entities" : qUnion([Q0]), "operationType" : NewBodyOperationType.ADD, "endBound" : BoundingType.SYMMETRIC, "depth" : 28.57 * mm, "offsetDistance" : 25.4 * mm});
        }
        {
            var Q0;
            Q0=makeQuery(id+"F29.imprint","IMPRINT",FACE,{"disambiguationData":[TD([[makeQuery(id+"F29.imprint","IMPRINT",EDGE,{"derivedFrom":sQuery(id+"F29.wireOp",EDGE,"E471")}),1.0]])]});
            extrude(context, id + "F93", {"entities" : qUnion([Q0]), "operationType" : NewBodyOperationType.ADD, "endBound" : BoundingType.SYMMETRIC, "depth" : 63.5 * mm, "offsetDistance" : 25.4 * mm});
        }
        {
            var Q0;
            Q0=makeQuery(id+"F0.imprint","IMPRINT",FACE,{"disambiguationData":[TD([[makeQuery(id+"F0.imprint","IMPRINT",EDGE,{"derivedFrom":sQuery(id+"F0.wireOp",EDGE,"E42")}),1.0]])]});
            extrude(context, id + "F94", {"entities" : qUnion([Q0]), "operationType" : NewBodyOperationType.REMOVE, "oppositeDirection" : true, "depth" : 14.29 * mm, "offsetDistance" : 25.4 * mm});
        }
        {
            var Q0;
            Q0=makeQuery(id+"F0.imprint","IMPRINT",FACE,{"disambiguationData":[TD([[makeQuery(id+"F0.imprint","IMPRINT",EDGE,{"derivedFrom":sQuery(id+"F0.wireOp",EDGE,"E49")}),1.0]])]});
            extrude(context, id + "F95", {"entities" : qUnion([Q0]), "oppositeDirection" : true, "depth" : 14.29 * mm, "offsetDistance" : 25.4 * mm});
        }
        {
            var Q0;
            Q0=makeQuery(id+"F0.imprint","IMPRINT",FACE,{"disambiguationData":[TD([[makeQuery(id+"F0.imprint","IMPRINT",EDGE,{"derivedFrom":sQuery(id+"F0.wireOp",EDGE,"E48")}),1.0]])]});
            extrude(context, id + "F96", {"entities" : qUnion([Q0]), "operationType" : NewBodyOperationType.ADD, "oppositeDirection" : true, "depth" : 31.75 * mm, "offsetDistance" : 25.4 * mm});
        }
        {
            var Q0;
            Q0=makeQuery(id+"F29.imprint","IMPRINT",FACE,{"disambiguationData":[TD([[makeQuery(id+"F29.imprint","IMPRINT",EDGE,{"derivedFrom":sQuery(id+"F29.wireOp",EDGE,"E461")}),1.0]])]});
            extrude(context, id + "F97", {"entities" : qUnion([Q0]), "operationType" : NewBodyOperationType.REMOVE, "endBound" : BoundingType.SYMMETRIC, "oppositeDirection" : true, "depth" : 28.57 * mm, "offsetDistance" : 25.4 * mm});
        }
        {
            var Q0;
            Q0=makeQuery(id+"F29.imprint","IMPRINT",FACE,{"disambiguationData":[TD([[makeQuery(id+"F29.imprint","IMPRINT",EDGE,{"derivedFrom":sQuery(id+"F29.wireOp",EDGE,"E460")}),1.0]])]});
            extrude(context, id + "F98", {"entities" : qUnion([Q0]), "operationType" : NewBodyOperationType.ADD, "endBound" : BoundingType.SYMMETRIC, "depth" : 28.57 * mm, "offsetDistance" : 25.4 * mm});
        }
        {
            var Q0;
            Q0=makeQuery(id+"F29.imprint","IMPRINT",FACE,{"disambiguationData":[TD([[makeQuery(id+"F29.imprint","IMPRINT",EDGE,{"derivedFrom":sQuery(id+"F29.wireOp",EDGE,"E459")}),1.0]])]});
            extrude(context, id + "F99", {"entities" : qUnion([Q0]), "operationType" : NewBodyOperationType.ADD, "endBound" : BoundingType.SYMMETRIC, "depth" : 63.5 * mm, "offsetDistance" : 25.4 * mm});
        }
        {
            var Q0;
            Q0=makeQuery(id+"F0.imprint","IMPRINT",FACE,{"disambiguationData":[TD([[makeQuery(id+"F0.imprint","IMPRINT",EDGE,{"derivedFrom":sQuery(id+"F0.wireOp",EDGE,"E50")}),1.0]])]});
            extrude(context, id + "F100", {"entities" : qUnion([Q0]), "operationType" : NewBodyOperationType.REMOVE, "oppositeDirection" : true, "depth" : 14.29 * mm, "offsetDistance" : 25.4 * mm});
        }
        {
            var Q0;
            Q0=makeQuery(id+"F20.imprint","IMPRINT",FACE,{"disambiguationData":[TD([[makeQuery(id+"F20.imprint","IMPRINT",EDGE,{"derivedFrom":sQuery(id+"F20.wireOp",EDGE,"E167")}),1.0]])]});
            extrude(context, id + "F101", {"entities" : qUnion([Q0]), "oppositeDirection" : true, "depth" : 14.29 * mm, "offsetDistance" : 25.4 * mm});
        }
        {
            var Q0;
            Q0=makeQuery(id+"F20.imprint","IMPRINT",FACE,{"disambiguationData":[TD([[makeQuery(id+"F20.imprint","IMPRINT",EDGE,{"derivedFrom":sQuery(id+"F20.wireOp",EDGE,"E166")}),1.0]])]});
            extrude(context, id + "F102", {"entities" : qUnion([Q0]), "operationType" : NewBodyOperationType.ADD, "oppositeDirection" : true, "depth" : 31.75 * mm, "offsetDistance" : 25.4 * mm});
        }
        {
            var Q0;
            Q0=makeQuery(id+"F27.imprint","IMPRINT",FACE,{"disambiguationData":[TD([[makeQuery(id+"F27.imprint","IMPRINT",EDGE,{"derivedFrom":sQuery(id+"F27.wireOp",EDGE,"E361")}),1.0]])]});
            extrude(context, id + "F103", {"entities" : qUnion([Q0]), "operationType" : NewBodyOperationType.REMOVE, "endBound" : BoundingType.SYMMETRIC, "depth" : 28.57 * mm, "offsetDistance" : 25.4 * mm});
        }
        {
            var Q0;
            Q0=makeQuery(id+"F27.imprint","IMPRINT",FACE,{"disambiguationData":[TD([[makeQuery(id+"F27.imprint","IMPRINT",EDGE,{"derivedFrom":sQuery(id+"F27.wireOp",EDGE,"E360")}),1.0]])]});
            extrude(context, id + "F104", {"entities" : qUnion([Q0]), "operationType" : NewBodyOperationType.ADD, "endBound" : BoundingType.SYMMETRIC, "depth" : 28.57 * mm, "offsetDistance" : 25.4 * mm});
        }
        {
            var Q0;
            Q0=makeQuery(id+"F27.imprint","IMPRINT",FACE,{"disambiguationData":[TD([[makeQuery(id+"F27.imprint","IMPRINT",EDGE,{"derivedFrom":sQuery(id+"F27.wireOp",EDGE,"E359")}),1.0]])]});
            extrude(context, id + "F105", {"entities" : qUnion([Q0]), "operationType" : NewBodyOperationType.ADD, "endBound" : BoundingType.SYMMETRIC, "depth" : 63.5 * mm, "offsetDistance" : 25.4 * mm});
        }
        {
            var Q0;
            Q0=makeQuery(id+"F20.imprint","IMPRINT",FACE,{"disambiguationData":[TD([[makeQuery(id+"F20.imprint","IMPRINT",EDGE,{"derivedFrom":sQuery(id+"F20.wireOp",EDGE,"E168")}),1.0]])]});
            extrude(context, id + "F106", {"entities" : qUnion([Q0]), "operationType" : NewBodyOperationType.REMOVE, "oppositeDirection" : true, "depth" : 14.29 * mm, "offsetDistance" : 25.4 * mm});
        }
        {
            var Q0;
            Q0=makeQuery(id+"F27.imprint","IMPRINT",FACE,{"disambiguationData":[TD([[makeQuery(id+"F27.imprint","IMPRINT",EDGE,{"derivedFrom":sQuery(id+"F27.wireOp",EDGE,"E380")}),1.0]])]});
            extrude(context, id + "F107", {"entities" : qUnion([Q0]), "depth" : 14.29 * mm, "offsetDistance" : 25.4 * mm});
        }
        {
            var Q0;
            Q0=makeQuery(id+"F27.imprint","IMPRINT",FACE,{"disambiguationData":[TD([[makeQuery(id+"F27.imprint","IMPRINT",EDGE,{"derivedFrom":sQuery(id+"F27.wireOp",EDGE,"E379")}),1.0]])]});
            extrude(context, id + "F108", {"entities" : qUnion([Q0]), "operationType" : NewBodyOperationType.ADD, "depth" : 31.75 * mm, "offsetDistance" : 25.4 * mm});
        }
        {
            var Q0;
            Q0=makeQuery(id+"F18.imprint","IMPRINT",FACE,{"disambiguationData":[TD([[makeQuery(id+"F18.imprint","IMPRINT",EDGE,{"derivedFrom":sQuery(id+"F18.wireOp",EDGE,"E139")}),1.0]])]});
            extrude(context, id + "F109", {"entities" : qUnion([Q0]), "operationType" : NewBodyOperationType.REMOVE, "endBound" : BoundingType.SYMMETRIC, "depth" : 28.57 * mm, "offsetDistance" : 25.4 * mm});
        }
        {
            var Q0;
            Q0=makeQuery(id+"F18.imprint","IMPRINT",FACE,{"disambiguationData":[TD([[makeQuery(id+"F18.imprint","IMPRINT",EDGE,{"derivedFrom":sQuery(id+"F18.wireOp",EDGE,"E138")}),1.0]])]});
            extrude(context, id + "F110", {"entities" : qUnion([Q0]), "operationType" : NewBodyOperationType.ADD, "endBound" : BoundingType.SYMMETRIC, "depth" : 28.57 * mm, "offsetDistance" : 25.4 * mm});
        }
        {
            var Q0;
            Q0=makeQuery(id+"F18.imprint","IMPRINT",FACE,{"disambiguationData":[TD([[makeQuery(id+"F18.imprint","IMPRINT",EDGE,{"derivedFrom":sQuery(id+"F18.wireOp",EDGE,"E137")}),1.0]])]});
            extrude(context, id + "F111", {"entities" : qUnion([Q0]), "operationType" : NewBodyOperationType.ADD, "endBound" : BoundingType.SYMMETRIC, "depth" : 63.5 * mm, "offsetDistance" : 25.4 * mm});
        }
        {
            var Q0;
            Q0=makeQuery(id+"F27.imprint","IMPRINT",FACE,{"disambiguationData":[TD([[makeQuery(id+"F27.imprint","IMPRINT",EDGE,{"derivedFrom":sQuery(id+"F27.wireOp",EDGE,"E381")}),1.0]])]});
            extrude(context, id + "F112", {"entities" : qUnion([Q0]), "operationType" : NewBodyOperationType.REMOVE, "depth" : 14.29 * mm, "offsetDistance" : 25.4 * mm});
        }
        {
            var Q0;
            Q0=makeQuery(id+"F27.imprint","IMPRINT",FACE,{"disambiguationData":[TD([[makeQuery(id+"F27.imprint","IMPRINT",EDGE,{"derivedFrom":sQuery(id+"F27.wireOp",EDGE,"E352")}),1.0]])]});
            extrude(context, id + "F113", {"entities" : qUnion([Q0]), "depth" : 14.29 * mm, "offsetDistance" : 25.4 * mm});
        }
        {
            var Q0;
            Q0=makeQuery(id+"F27.imprint","IMPRINT",FACE,{"disambiguationData":[TD([[makeQuery(id+"F27.imprint","IMPRINT",EDGE,{"derivedFrom":sQuery(id+"F27.wireOp",EDGE,"E351")}),1.0]])]});
            extrude(context, id + "F114", {"entities" : qUnion([Q0]), "operationType" : NewBodyOperationType.ADD, "depth" : 31.75 * mm, "offsetDistance" : 25.4 * mm});
        }
        {
            var Q0;
            Q0=makeQuery(id+"F15.imprint","IMPRINT",FACE,{"disambiguationData":[TD([[makeQuery(id+"F15.imprint","IMPRINT",EDGE,{"derivedFrom":sQuery(id+"F15.wireOp",EDGE,"E104")}),1.0]])]});
            extrude(context, id + "F115", {"entities" : qUnion([Q0]), "operationType" : NewBodyOperationType.REMOVE, "endBound" : BoundingType.SYMMETRIC, "oppositeDirection" : true, "depth" : 28.57 * mm, "offsetDistance" : 25.4 * mm});
        }
        {
            var Q0;
            Q0=makeQuery(id+"F15.imprint","IMPRINT",FACE,{"disambiguationData":[TD([[makeQuery(id+"F15.imprint","IMPRINT",EDGE,{"derivedFrom":sQuery(id+"F15.wireOp",EDGE,"E103")}),1.0]])]});
            extrude(context, id + "F116", {"entities" : qUnion([Q0]), "operationType" : NewBodyOperationType.ADD, "endBound" : BoundingType.SYMMETRIC, "depth" : 28.57 * mm, "offsetDistance" : 25.4 * mm});
        }
        {
            var Q0;
            Q0=makeQuery(id+"F15.imprint","IMPRINT",FACE,{"disambiguationData":[TD([[makeQuery(id+"F15.imprint","IMPRINT",EDGE,{"derivedFrom":sQuery(id+"F15.wireOp",EDGE,"E102")}),1.0]])]});
            extrude(context, id + "F117", {"entities" : qUnion([Q0]), "operationType" : NewBodyOperationType.ADD, "endBound" : BoundingType.SYMMETRIC, "depth" : 63.5 * mm, "offsetDistance" : 25.4 * mm});
        }
        {
            var Q0;
            Q0=makeQuery(id+"F27.imprint","IMPRINT",FACE,{"disambiguationData":[TD([[makeQuery(id+"F27.imprint","IMPRINT",EDGE,{"derivedFrom":sQuery(id+"F27.wireOp",EDGE,"E353")}),1.0]])]});
            extrude(context, id + "F118", {"entities" : qUnion([Q0]), "operationType" : NewBodyOperationType.REMOVE, "depth" : 14.29 * mm, "offsetDistance" : 25.4 * mm});
        }
        {
            var Q0;
            Q0=makeQuery(id+"F15.imprint","IMPRINT",FACE,{"disambiguationData":[TD([[makeQuery(id+"F15.imprint","IMPRINT",EDGE,{"derivedFrom":sQuery(id+"F15.wireOp",EDGE,"E99")}),1.0]])]});
            extrude(context, id + "F119", {"entities" : qUnion([Q0]), "oppositeDirection" : true, "depth" : 14.29 * mm, "offsetDistance" : 25.4 * mm});
        }
        {
            var Q0;
            Q0=makeQuery(id+"F15.imprint","IMPRINT",FACE,{"disambiguationData":[TD([[makeQuery(id+"F15.imprint","IMPRINT",EDGE,{"derivedFrom":sQuery(id+"F15.wireOp",EDGE,"E98")}),1.0]])]});
            extrude(context, id + "F120", {"entities" : qUnion([Q0]), "operationType" : NewBodyOperationType.ADD, "oppositeDirection" : true, "depth" : 31.75 * mm, "offsetDistance" : 25.4 * mm});
        }
        {
            var Q0;
            Q0=makeQuery(id+"F31.imprint","IMPRINT",FACE,{"disambiguationData":[TD([[makeQuery(id+"F31.imprint","IMPRINT",EDGE,{"derivedFrom":sQuery(id+"F31.wireOp",EDGE,"E493")}),1.0]])]});
            extrude(context, id + "F121", {"entities" : qUnion([Q0]), "operationType" : NewBodyOperationType.REMOVE, "endBound" : BoundingType.SYMMETRIC, "oppositeDirection" : true, "depth" : 28.57 * mm, "offsetDistance" : 25.4 * mm});
        }
        {
            var Q0;
            Q0=makeQuery(id+"F31.imprint","IMPRINT",FACE,{"disambiguationData":[TD([[makeQuery(id+"F31.imprint","IMPRINT",EDGE,{"derivedFrom":sQuery(id+"F31.wireOp",EDGE,"E492")}),1.0]])]});
            extrude(context, id + "F122", {"entities" : qUnion([Q0]), "operationType" : NewBodyOperationType.ADD, "endBound" : BoundingType.SYMMETRIC, "depth" : 28.57 * mm, "offsetDistance" : 25.4 * mm});
        }
        {
            var Q0;
            Q0=makeQuery(id+"F31.imprint","IMPRINT",FACE,{"disambiguationData":[TD([[makeQuery(id+"F31.imprint","IMPRINT",EDGE,{"derivedFrom":sQuery(id+"F31.wireOp",EDGE,"E491")}),1.0]])]});
            extrude(context, id + "F123", {"entities" : qUnion([Q0]), "operationType" : NewBodyOperationType.ADD, "endBound" : BoundingType.SYMMETRIC, "depth" : 63.5 * mm, "offsetDistance" : 25.4 * mm});
        }
        {
            var Q0;
            Q0=makeQuery(id+"F15.imprint","IMPRINT",FACE,{"disambiguationData":[TD([[makeQuery(id+"F15.imprint","IMPRINT",EDGE,{"derivedFrom":sQuery(id+"F15.wireOp",EDGE,"E100")}),1.0]])]});
            extrude(context, id + "F124", {"entities" : qUnion([Q0]), "operationType" : NewBodyOperationType.REMOVE, "oppositeDirection" : true, "depth" : 14.29 * mm, "offsetDistance" : 25.4 * mm});
        }
        {
            var Q0;
            Q0=makeQuery(id+"F33.imprint","IMPRINT",FACE,{"disambiguationData":[TD([[makeQuery(id+"F33.imprint","IMPRINT",EDGE,{"derivedFrom":sQuery(id+"F33.wireOp",EDGE,"E524")}),1.0]])]});
            extrude(context, id + "F125", {"entities" : qUnion([Q0]), "oppositeDirection" : true, "depth" : 14.29 * mm, "offsetDistance" : 25.4 * mm});
        }
        {
            var Q0;
            Q0=makeQuery(id+"F33.imprint","IMPRINT",FACE,{"disambiguationData":[TD([[makeQuery(id+"F33.imprint","IMPRINT",EDGE,{"derivedFrom":sQuery(id+"F33.wireOp",EDGE,"E523")}),1.0]])]});
            extrude(context, id + "F126", {"entities" : qUnion([Q0]), "operationType" : NewBodyOperationType.ADD, "oppositeDirection" : true, "depth" : 31.75 * mm, "offsetDistance" : 25.4 * mm});
        }
        {
            var Q0;
            Q0=makeQuery(id+"F24.imprint","IMPRINT",FACE,{"disambiguationData":[TD([[makeQuery(id+"F24.imprint","IMPRINT",EDGE,{"derivedFrom":sQuery(id+"F24.wireOp",EDGE,"E280")}),1.0]])]});
            extrude(context, id + "F127", {"entities" : qUnion([Q0]), "operationType" : NewBodyOperationType.REMOVE, "endBound" : BoundingType.SYMMETRIC, "depth" : 28.57 * mm, "offsetDistance" : 25.4 * mm});
        }
        {
            var Q0;
            Q0=makeQuery(id+"F24.imprint","IMPRINT",FACE,{"disambiguationData":[TD([[makeQuery(id+"F24.imprint","IMPRINT",EDGE,{"derivedFrom":sQuery(id+"F24.wireOp",EDGE,"E279")}),1.0]])]});
            extrude(context, id + "F128", {"entities" : qUnion([Q0]), "operationType" : NewBodyOperationType.ADD, "endBound" : BoundingType.SYMMETRIC, "depth" : 28.57 * mm, "offsetDistance" : 25.4 * mm});
        }
        {
            var Q0;
            Q0=makeQuery(id+"F24.imprint","IMPRINT",FACE,{"disambiguationData":[TD([[makeQuery(id+"F24.imprint","IMPRINT",EDGE,{"derivedFrom":sQuery(id+"F24.wireOp",EDGE,"E278")}),1.0]])]});
            extrude(context, id + "F129", {"entities" : qUnion([Q0]), "operationType" : NewBodyOperationType.ADD, "endBound" : BoundingType.SYMMETRIC, "depth" : 63.5 * mm, "offsetDistance" : 25.4 * mm});
        }
        {
            var Q0;
            Q0=makeQuery(id+"F33.imprint","IMPRINT",FACE,{"disambiguationData":[TD([[makeQuery(id+"F33.imprint","IMPRINT",EDGE,{"derivedFrom":sQuery(id+"F33.wireOp",EDGE,"E525")}),1.0]])]});
            extrude(context, id + "F130", {"entities" : qUnion([Q0]), "operationType" : NewBodyOperationType.REMOVE, "oppositeDirection" : true, "depth" : 14.29 * mm, "offsetDistance" : 25.4 * mm});
        }
        {
            var Q0;
            Q0=makeQuery(id+"F29.imprint","IMPRINT",FACE,{"disambiguationData":[TD([[makeQuery(id+"F29.imprint","IMPRINT",EDGE,{"derivedFrom":sQuery(id+"F29.wireOp",EDGE,"E448")}),1.0]])]});
            extrude(context, id + "F131", {"entities" : qUnion([Q0]), "depth" : 14.29 * mm, "offsetDistance" : 25.4 * mm});
        }
        {
            var Q0;
            Q0=makeQuery(id+"F29.imprint","IMPRINT",FACE,{"disambiguationData":[TD([[makeQuery(id+"F29.imprint","IMPRINT",EDGE,{"derivedFrom":sQuery(id+"F29.wireOp",EDGE,"E447")}),1.0]])]});
            extrude(context, id + "F132", {"entities" : qUnion([Q0]), "operationType" : NewBodyOperationType.ADD, "depth" : 31.75 * mm, "offsetDistance" : 25.4 * mm});
        }
        {
            var Q0;
            Q0=makeQuery(id+"F24.imprint","IMPRINT",FACE,{"disambiguationData":[TD([[makeQuery(id+"F24.imprint","IMPRINT",EDGE,{"derivedFrom":sQuery(id+"F24.wireOp",EDGE,"E276")}),1.0]])]});
            extrude(context, id + "F133", {"entities" : qUnion([Q0]), "operationType" : NewBodyOperationType.REMOVE, "endBound" : BoundingType.SYMMETRIC, "oppositeDirection" : true, "depth" : 28.57 * mm, "offsetDistance" : 25.4 * mm});
        }
        {
            var Q0;
            Q0=makeQuery(id+"F24.imprint","IMPRINT",FACE,{"disambiguationData":[TD([[makeQuery(id+"F24.imprint","IMPRINT",EDGE,{"derivedFrom":sQuery(id+"F24.wireOp",EDGE,"E275")}),1.0]])]});
            extrude(context, id + "F134", {"entities" : qUnion([Q0]), "operationType" : NewBodyOperationType.ADD, "endBound" : BoundingType.SYMMETRIC, "depth" : 28.57 * mm, "offsetDistance" : 25.4 * mm});
        }
        {
            var Q0;
            Q0=makeQuery(id+"F24.imprint","IMPRINT",FACE,{"disambiguationData":[TD([[makeQuery(id+"F24.imprint","IMPRINT",EDGE,{"derivedFrom":sQuery(id+"F24.wireOp",EDGE,"E274")}),1.0]])]});
            extrude(context, id + "F135", {"entities" : qUnion([Q0]), "operationType" : NewBodyOperationType.ADD, "endBound" : BoundingType.SYMMETRIC, "depth" : 63.5 * mm, "offsetDistance" : 25.4 * mm});
        }
        {
            var Q0;
            Q0=makeQuery(id+"F29.imprint","IMPRINT",FACE,{"disambiguationData":[TD([[makeQuery(id+"F29.imprint","IMPRINT",EDGE,{"derivedFrom":sQuery(id+"F29.wireOp",EDGE,"E449")}),1.0]])]});
            extrude(context, id + "F136", {"entities" : qUnion([Q0]), "operationType" : NewBodyOperationType.REMOVE, "depth" : 14.29 * mm, "offsetDistance" : 25.4 * mm});
        }
        {
            var Q0;
            Q0=makeQuery(id+"F26.imprint","IMPRINT",FACE,{"disambiguationData":[TD([[makeQuery(id+"F26.imprint","IMPRINT",EDGE,{"derivedFrom":sQuery(id+"F26.wireOp",EDGE,"E312")}),1.0]])]});
            extrude(context, id + "F137", {"entities" : qUnion([Q0]), "depth" : 14.29 * mm, "offsetDistance" : 25.4 * mm});
        }
        {
            var Q0;
            Q0=makeQuery(id+"F26.imprint","IMPRINT",FACE,{"disambiguationData":[TD([[makeQuery(id+"F26.imprint","IMPRINT",EDGE,{"derivedFrom":sQuery(id+"F26.wireOp",EDGE,"E311")}),1.0]])]});
            extrude(context, id + "F138", {"entities" : qUnion([Q0]), "operationType" : NewBodyOperationType.ADD, "depth" : 31.75 * mm, "offsetDistance" : 25.4 * mm});
        }
        {
            var Q0;
            Q0=makeQuery(id+"F29.imprint","IMPRINT",FACE,{"disambiguationData":[TD([[makeQuery(id+"F29.imprint","IMPRINT",EDGE,{"derivedFrom":sQuery(id+"F29.wireOp",EDGE,"E453")}),1.0]])]});
            extrude(context, id + "F139", {"entities" : qUnion([Q0]), "operationType" : NewBodyOperationType.REMOVE, "endBound" : BoundingType.SYMMETRIC, "oppositeDirection" : true, "depth" : 28.57 * mm, "offsetDistance" : 25.4 * mm});
        }
        {
            var Q0;
            Q0=makeQuery(id+"F29.imprint","IMPRINT",FACE,{"disambiguationData":[TD([[makeQuery(id+"F29.imprint","IMPRINT",EDGE,{"derivedFrom":sQuery(id+"F29.wireOp",EDGE,"E452")}),1.0]])]});
            extrude(context, id + "F140", {"entities" : qUnion([Q0]), "operationType" : NewBodyOperationType.ADD, "endBound" : BoundingType.SYMMETRIC, "depth" : 28.57 * mm, "offsetDistance" : 25.4 * mm});
        }
        {
            var Q0;
            Q0=makeQuery(id+"F29.imprint","IMPRINT",FACE,{"disambiguationData":[TD([[makeQuery(id+"F29.imprint","IMPRINT",EDGE,{"derivedFrom":sQuery(id+"F29.wireOp",EDGE,"E451")}),1.0]])]});
            extrude(context, id + "F141", {"entities" : qUnion([Q0]), "operationType" : NewBodyOperationType.ADD, "endBound" : BoundingType.SYMMETRIC, "depth" : 63.5 * mm, "offsetDistance" : 25.4 * mm});
        }
        {
            var Q0;
            Q0=makeQuery(id+"F26.imprint","IMPRINT",FACE,{"disambiguationData":[TD([[makeQuery(id+"F26.imprint","IMPRINT",EDGE,{"derivedFrom":sQuery(id+"F26.wireOp",EDGE,"E313")}),1.0]])]});
            extrude(context, id + "F142", {"entities" : qUnion([Q0]), "operationType" : NewBodyOperationType.REMOVE, "depth" : 14.29 * mm, "offsetDistance" : 25.4 * mm});
        }
        {
            var Q0;
            Q0=makeQuery(id+"F26.imprint","IMPRINT",FACE,{"disambiguationData":[TD([[makeQuery(id+"F26.imprint","IMPRINT",EDGE,{"derivedFrom":sQuery(id+"F26.wireOp",EDGE,"E304")}),1.0]])]});
            extrude(context, id + "F143", {"entities" : qUnion([Q0]), "depth" : 14.29 * mm, "offsetDistance" : 25.4 * mm});
        }
        {
            var Q0;
            Q0=makeQuery(id+"F26.imprint","IMPRINT",FACE,{"disambiguationData":[TD([[makeQuery(id+"F26.imprint","IMPRINT",EDGE,{"derivedFrom":sQuery(id+"F26.wireOp",EDGE,"E303")}),1.0]])]});
            extrude(context, id + "F144", {"entities" : qUnion([Q0]), "operationType" : NewBodyOperationType.ADD, "depth" : 31.75 * mm, "offsetDistance" : 25.4 * mm});
        }
        {
            var Q0;
            Q0=makeQuery(id+"F29.imprint","IMPRINT",FACE,{"disambiguationData":[TD([[makeQuery(id+"F29.imprint","IMPRINT",EDGE,{"derivedFrom":sQuery(id+"F29.wireOp",EDGE,"E457")}),1.0]])]});
            extrude(context, id + "F145", {"entities" : qUnion([Q0]), "operationType" : NewBodyOperationType.REMOVE, "endBound" : BoundingType.SYMMETRIC, "oppositeDirection" : true, "depth" : 28.57 * mm, "offsetDistance" : 25.4 * mm});
        }
        {
            var Q0;
            Q0=makeQuery(id+"F29.imprint","IMPRINT",FACE,{"disambiguationData":[TD([[makeQuery(id+"F29.imprint","IMPRINT",EDGE,{"derivedFrom":sQuery(id+"F29.wireOp",EDGE,"E456")}),1.0]])]});
            extrude(context, id + "F146", {"entities" : qUnion([Q0]), "operationType" : NewBodyOperationType.ADD, "endBound" : BoundingType.SYMMETRIC, "depth" : 28.57 * mm, "offsetDistance" : 25.4 * mm});
        }
        {
            var Q0;
            Q0=makeQuery(id+"F29.imprint","IMPRINT",FACE,{"disambiguationData":[TD([[makeQuery(id+"F29.imprint","IMPRINT",EDGE,{"derivedFrom":sQuery(id+"F29.wireOp",EDGE,"E455")}),1.0]])]});
            extrude(context, id + "F147", {"entities" : qUnion([Q0]), "operationType" : NewBodyOperationType.ADD, "endBound" : BoundingType.SYMMETRIC, "depth" : 63.5 * mm, "offsetDistance" : 25.4 * mm});
        }
        {
            var Q0;
            Q0=makeQuery(id+"F26.imprint","IMPRINT",FACE,{"disambiguationData":[TD([[makeQuery(id+"F26.imprint","IMPRINT",EDGE,{"derivedFrom":sQuery(id+"F26.wireOp",EDGE,"E305")}),1.0]])]});
            extrude(context, id + "F148", {"entities" : qUnion([Q0]), "operationType" : NewBodyOperationType.REMOVE, "depth" : 14.29 * mm, "offsetDistance" : 25.4 * mm});
        }
        {
            var Q0;
            Q0=makeQuery(id+"F26.imprint","IMPRINT",FACE,{"disambiguationData":[TD([[makeQuery(id+"F26.imprint","IMPRINT",EDGE,{"derivedFrom":sQuery(id+"F26.wireOp",EDGE,"E316")}),1.0]])]});
            extrude(context, id + "F149", {"entities" : qUnion([Q0]), "depth" : 14.29 * mm, "offsetDistance" : 25.4 * mm});
        }
        {
            var Q0;
            Q0=makeQuery(id+"F26.imprint","IMPRINT",FACE,{"disambiguationData":[TD([[makeQuery(id+"F26.imprint","IMPRINT",EDGE,{"derivedFrom":sQuery(id+"F26.wireOp",EDGE,"E315")}),1.0]])]});
            extrude(context, id + "F150", {"entities" : qUnion([Q0]), "operationType" : NewBodyOperationType.ADD, "depth" : 31.75 * mm, "offsetDistance" : 25.4 * mm});
        }
        {
            var Q0;
            Q0=makeQuery(id+"F29.imprint","IMPRINT",FACE,{"disambiguationData":[TD([[makeQuery(id+"F29.imprint","IMPRINT",EDGE,{"derivedFrom":sQuery(id+"F29.wireOp",EDGE,"E469")}),1.0]])]});
            extrude(context, id + "F151", {"entities" : qUnion([Q0]), "operationType" : NewBodyOperationType.REMOVE, "endBound" : BoundingType.SYMMETRIC, "oppositeDirection" : true, "depth" : 28.57 * mm, "offsetDistance" : 25.4 * mm});
        }
        {
            var Q0;
            Q0=makeQuery(id+"F29.imprint","IMPRINT",FACE,{"disambiguationData":[TD([[makeQuery(id+"F29.imprint","IMPRINT",EDGE,{"derivedFrom":sQuery(id+"F29.wireOp",EDGE,"E468")}),1.0]])]});
            extrude(context, id + "F152", {"entities" : qUnion([Q0]), "operationType" : NewBodyOperationType.ADD, "endBound" : BoundingType.SYMMETRIC, "depth" : 28.57 * mm, "offsetDistance" : 25.4 * mm});
        }
        {
            var Q0;
            Q0=makeQuery(id+"F29.imprint","IMPRINT",FACE,{"disambiguationData":[TD([[makeQuery(id+"F29.imprint","IMPRINT",EDGE,{"derivedFrom":sQuery(id+"F29.wireOp",EDGE,"E467")}),1.0]])]});
            extrude(context, id + "F153", {"entities" : qUnion([Q0]), "operationType" : NewBodyOperationType.ADD, "endBound" : BoundingType.SYMMETRIC, "depth" : 63.5 * mm, "offsetDistance" : 25.4 * mm});
        }
        {
            var Q0;
            Q0=makeQuery(id+"F26.imprint","IMPRINT",FACE,{"disambiguationData":[TD([[makeQuery(id+"F26.imprint","IMPRINT",EDGE,{"derivedFrom":sQuery(id+"F26.wireOp",EDGE,"E317")}),1.0]])]});
            extrude(context, id + "F154", {"entities" : qUnion([Q0]), "operationType" : NewBodyOperationType.REMOVE, "depth" : 14.29 * mm, "offsetDistance" : 25.4 * mm});
        }
        {
            var Q0;
            Q0=makeQuery(id+"F29.imprint","IMPRINT",FACE,{"disambiguationData":[TD([[makeQuery(id+"F29.imprint","IMPRINT",EDGE,{"derivedFrom":sQuery(id+"F29.wireOp",EDGE,"E440")}),1.0]])]});
            extrude(context, id + "F155", {"entities" : qUnion([Q0]), "depth" : 14.29 * mm, "offsetDistance" : 25.4 * mm});
        }
        {
            var Q0;
            Q0=makeQuery(id+"F29.imprint","IMPRINT",FACE,{"disambiguationData":[TD([[makeQuery(id+"F29.imprint","IMPRINT",EDGE,{"derivedFrom":sQuery(id+"F29.wireOp",EDGE,"E439")}),1.0]])]});
            extrude(context, id + "F156", {"entities" : qUnion([Q0]), "operationType" : NewBodyOperationType.ADD, "depth" : 31.75 * mm, "offsetDistance" : 25.4 * mm});
        }
        {
            var Q0;
            Q0=makeQuery(id+"F24.imprint","IMPRINT",FACE,{"disambiguationData":[TD([[makeQuery(id+"F24.imprint","IMPRINT",EDGE,{"derivedFrom":sQuery(id+"F24.wireOp",EDGE,"E284")}),1.0]])]});
            extrude(context, id + "F157", {"entities" : qUnion([Q0]), "operationType" : NewBodyOperationType.REMOVE, "endBound" : BoundingType.SYMMETRIC, "oppositeDirection" : true, "depth" : 28.57 * mm, "offsetDistance" : 25.4 * mm});
        }
        {
            var Q0;
            Q0=makeQuery(id+"F24.imprint","IMPRINT",FACE,{"disambiguationData":[TD([[makeQuery(id+"F24.imprint","IMPRINT",EDGE,{"derivedFrom":sQuery(id+"F24.wireOp",EDGE,"E283")}),1.0]])]});
            extrude(context, id + "F158", {"entities" : qUnion([Q0]), "operationType" : NewBodyOperationType.ADD, "endBound" : BoundingType.SYMMETRIC, "oppositeDirection" : true, "depth" : 28.57 * mm, "offsetDistance" : 25.4 * mm});
        }
        {
            var Q0;
            Q0=makeQuery(id+"F24.imprint","IMPRINT",FACE,{"disambiguationData":[TD([[makeQuery(id+"F24.imprint","IMPRINT",EDGE,{"derivedFrom":sQuery(id+"F24.wireOp",EDGE,"E282")}),1.0]])]});
            extrude(context, id + "F159", {"entities" : qUnion([Q0]), "operationType" : NewBodyOperationType.ADD, "endBound" : BoundingType.SYMMETRIC, "depth" : 63.5 * mm, "offsetDistance" : 25.4 * mm});
        }
        {
            var Q0;
            Q0=makeQuery(id+"F29.imprint","IMPRINT",FACE,{"disambiguationData":[TD([[makeQuery(id+"F29.imprint","IMPRINT",EDGE,{"derivedFrom":sQuery(id+"F29.wireOp",EDGE,"E441")}),1.0]])]});
            extrude(context, id + "F160", {"entities" : qUnion([Q0]), "operationType" : NewBodyOperationType.REMOVE, "depth" : 25.4 * mm, "offsetDistance" : 25.4 * mm});
        }
        {
            var Q0;
            Q0=makeQuery(id+"F20.imprint","IMPRINT",FACE,{"disambiguationData":[TD([[makeQuery(id+"F20.imprint","IMPRINT",EDGE,{"derivedFrom":sQuery(id+"F20.wireOp",EDGE,"E163")}),1.0]])]});
            extrude(context, id + "F161", {"entities" : qUnion([Q0]), "oppositeDirection" : true, "depth" : 14.29 * mm, "offsetDistance" : 25.4 * mm});
        }
        {
            var Q0;
            Q0=makeQuery(id+"F20.imprint","IMPRINT",FACE,{"disambiguationData":[TD([[makeQuery(id+"F20.imprint","IMPRINT",EDGE,{"derivedFrom":sQuery(id+"F20.wireOp",EDGE,"E162")}),1.0]])]});
            extrude(context, id + "F162", {"entities" : qUnion([Q0]), "operationType" : NewBodyOperationType.ADD, "oppositeDirection" : true, "depth" : 31.75 * mm, "offsetDistance" : 25.4 * mm});
        }
        {
            var Q0;
            Q0=makeQuery(id+"F31.imprint","IMPRINT",FACE,{"disambiguationData":[TD([[makeQuery(id+"F31.imprint","IMPRINT",EDGE,{"derivedFrom":sQuery(id+"F31.wireOp",EDGE,"E481")}),1.0]])]});
            extrude(context, id + "F163", {"entities" : qUnion([Q0]), "operationType" : NewBodyOperationType.REMOVE, "endBound" : BoundingType.SYMMETRIC, "oppositeDirection" : true, "depth" : 28.57 * mm, "offsetDistance" : 25.4 * mm});
        }
        {
            var Q0;
            Q0=makeQuery(id+"F31.imprint","IMPRINT",FACE,{"disambiguationData":[TD([[makeQuery(id+"F31.imprint","IMPRINT",EDGE,{"derivedFrom":sQuery(id+"F31.wireOp",EDGE,"E480")}),1.0]])]});
            extrude(context, id + "F164", {"entities" : qUnion([Q0]), "operationType" : NewBodyOperationType.ADD, "endBound" : BoundingType.SYMMETRIC, "depth" : 28.57 * mm, "offsetDistance" : 25.4 * mm});
        }
        {
            var Q0;
            Q0=makeQuery(id+"F31.imprint","IMPRINT",FACE,{"disambiguationData":[TD([[makeQuery(id+"F31.imprint","IMPRINT",EDGE,{"derivedFrom":sQuery(id+"F31.wireOp",EDGE,"E479")}),1.0]])]});
            extrude(context, id + "F165", {"entities" : qUnion([Q0]), "operationType" : NewBodyOperationType.ADD, "endBound" : BoundingType.SYMMETRIC, "depth" : 63.5 * mm, "offsetDistance" : 25.4 * mm});
        }
        {
            var Q0;
            Q0=makeQuery(id+"F20.imprint","IMPRINT",FACE,{"disambiguationData":[TD([[makeQuery(id+"F20.imprint","IMPRINT",EDGE,{"derivedFrom":sQuery(id+"F20.wireOp",EDGE,"E164")}),1.0]])]});
            extrude(context, id + "F166", {"entities" : qUnion([Q0]), "operationType" : NewBodyOperationType.REMOVE, "oppositeDirection" : true, "depth" : 14.29 * mm, "offsetDistance" : 25.4 * mm});
        }
        {
            var Q0;
            Q0=makeQuery(id+"F18.imprint","IMPRINT",FACE,{"disambiguationData":[TD([[makeQuery(id+"F18.imprint","IMPRINT",EDGE,{"derivedFrom":sQuery(id+"F18.wireOp",EDGE,"E130")}),1.0]])]});
            extrude(context, id + "F167", {"entities" : qUnion([Q0]), "depth" : 14.29 * mm, "offsetDistance" : 25.4 * mm});
        }
        {
            var Q0;
            Q0=makeQuery(id+"F18.imprint","IMPRINT",FACE,{"disambiguationData":[TD([[makeQuery(id+"F18.imprint","IMPRINT",EDGE,{"derivedFrom":sQuery(id+"F18.wireOp",EDGE,"E129")}),1.0]])]});
            extrude(context, id + "F168", {"entities" : qUnion([Q0]), "operationType" : NewBodyOperationType.ADD, "depth" : 31.75 * mm, "offsetDistance" : 25.4 * mm});
        }
        {
            var Q0;
            Q0=makeQuery(id+"F31.imprint","IMPRINT",FACE,{"disambiguationData":[TD([[makeQuery(id+"F31.imprint","IMPRINT",EDGE,{"derivedFrom":sQuery(id+"F31.wireOp",EDGE,"E505")}),1.0]])]});
            extrude(context, id + "F169", {"entities" : qUnion([Q0]), "operationType" : NewBodyOperationType.REMOVE, "endBound" : BoundingType.SYMMETRIC, "oppositeDirection" : true, "depth" : 28.57 * mm, "offsetDistance" : 25.4 * mm});
        }
        {
            var Q0;
            Q0=makeQuery(id+"F31.imprint","IMPRINT",FACE,{"disambiguationData":[TD([[makeQuery(id+"F31.imprint","IMPRINT",EDGE,{"derivedFrom":sQuery(id+"F31.wireOp",EDGE,"E504")}),1.0]])]});
            extrude(context, id + "F170", {"entities" : qUnion([Q0]), "operationType" : NewBodyOperationType.ADD, "endBound" : BoundingType.SYMMETRIC, "depth" : 28.57 * mm, "offsetDistance" : 25.4 * mm});
        }
        {
            var Q0;
            Q0=makeQuery(id+"F31.imprint","IMPRINT",FACE,{"disambiguationData":[TD([[makeQuery(id+"F31.imprint","IMPRINT",EDGE,{"derivedFrom":sQuery(id+"F31.wireOp",EDGE,"E503")}),1.0]])]});
            extrude(context, id + "F171", {"entities" : qUnion([Q0]), "operationType" : NewBodyOperationType.ADD, "endBound" : BoundingType.SYMMETRIC, "depth" : 63.5 * mm, "offsetDistance" : 25.4 * mm});
        }
        {
            var Q0;
            Q0=makeQuery(id+"F18.imprint","IMPRINT",FACE,{"disambiguationData":[TD([[makeQuery(id+"F18.imprint","IMPRINT",EDGE,{"derivedFrom":sQuery(id+"F18.wireOp",EDGE,"E131")}),1.0]])]});
            extrude(context, id + "F172", {"entities" : qUnion([Q0]), "operationType" : NewBodyOperationType.REMOVE, "depth" : 14.29 * mm, "offsetDistance" : 25.4 * mm});
        }
        {
            var Q0;
            Q0=makeQuery(id+"F33.imprint","IMPRINT",FACE,{"disambiguationData":[TD([[makeQuery(id+"F33.imprint","IMPRINT",EDGE,{"derivedFrom":sQuery(id+"F33.wireOp",EDGE,"E552")}),1.0]])]});
            extrude(context, id + "F173", {"entities" : qUnion([Q0]), "oppositeDirection" : true, "depth" : 14.29 * mm, "offsetDistance" : 25.4 * mm});
        }
        {
            var Q0;
            Q0=makeQuery(id+"F33.imprint","IMPRINT",FACE,{"disambiguationData":[TD([[makeQuery(id+"F33.imprint","IMPRINT",EDGE,{"derivedFrom":sQuery(id+"F33.wireOp",EDGE,"E551")}),1.0]])]});
            extrude(context, id + "F174", {"entities" : qUnion([Q0]), "operationType" : NewBodyOperationType.ADD, "oppositeDirection" : true, "depth" : 31.75 * mm, "offsetDistance" : 25.4 * mm});
        }
        {
            var Q0;
            Q0=makeQuery(id+"F24.imprint","IMPRINT",FACE,{"disambiguationData":[TD([[makeQuery(id+"F24.imprint","IMPRINT",EDGE,{"derivedFrom":sQuery(id+"F24.wireOp",EDGE,"E264")}),1.0]])]});
            extrude(context, id + "F175", {"entities" : qUnion([Q0]), "operationType" : NewBodyOperationType.REMOVE, "endBound" : BoundingType.SYMMETRIC, "oppositeDirection" : true, "depth" : 28.57 * mm, "offsetDistance" : 25.4 * mm});
        }
        {
            var Q0;
            Q0=makeQuery(id+"F24.imprint","IMPRINT",FACE,{"disambiguationData":[TD([[makeQuery(id+"F24.imprint","IMPRINT",EDGE,{"derivedFrom":sQuery(id+"F24.wireOp",EDGE,"E263")}),1.0]])]});
            extrude(context, id + "F176", {"entities" : qUnion([Q0]), "operationType" : NewBodyOperationType.ADD, "endBound" : BoundingType.SYMMETRIC, "depth" : 28.57 * mm, "offsetDistance" : 25.4 * mm});
        }
        {
            var Q0;
            Q0=makeQuery(id+"F24.imprint","IMPRINT",FACE,{"disambiguationData":[TD([[makeQuery(id+"F24.imprint","IMPRINT",EDGE,{"derivedFrom":sQuery(id+"F24.wireOp",EDGE,"E262")}),1.0]])]});
            extrude(context, id + "F177", {"entities" : qUnion([Q0]), "operationType" : NewBodyOperationType.ADD, "endBound" : BoundingType.SYMMETRIC, "depth" : 63.5 * mm, "offsetDistance" : 25.4 * mm});
        }
        {
            var Q0;
            Q0=makeQuery(id+"F33.imprint","IMPRINT",FACE,{"disambiguationData":[TD([[makeQuery(id+"F33.imprint","IMPRINT",EDGE,{"derivedFrom":sQuery(id+"F33.wireOp",EDGE,"E553")}),1.0]])]});
            extrude(context, id + "F178", {"entities" : qUnion([Q0]), "operationType" : NewBodyOperationType.REMOVE, "oppositeDirection" : true, "depth" : 14.29 * mm, "offsetDistance" : 25.4 * mm});
        }
        {
            var Q0;
            Q0=makeQuery(id+"F22.imprint","IMPRINT",FACE,{"disambiguationData":[TD([[makeQuery(id+"F22.imprint","IMPRINT",EDGE,{"derivedFrom":sQuery(id+"F22.wireOp",EDGE,"E187")}),1.0]])]});
            extrude(context, id + "F179", {"entities" : qUnion([Q0]), "oppositeDirection" : true, "depth" : 14.29 * mm, "offsetDistance" : 25.4 * mm});
        }
        {
            var Q0;
            Q0=makeQuery(id+"F22.imprint","IMPRINT",FACE,{"disambiguationData":[TD([[makeQuery(id+"F22.imprint","IMPRINT",EDGE,{"derivedFrom":sQuery(id+"F22.wireOp",EDGE,"E186")}),1.0]])]});
            extrude(context, id + "F180", {"entities" : qUnion([Q0]), "operationType" : NewBodyOperationType.ADD, "oppositeDirection" : true, "depth" : 31.75 * mm, "offsetDistance" : 25.4 * mm});
        }
        {
            var Q0;
            Q0=makeQuery(id+"F33.imprint","IMPRINT",FACE,{"disambiguationData":[TD([[makeQuery(id+"F33.imprint","IMPRINT",EDGE,{"derivedFrom":sQuery(id+"F33.wireOp",EDGE,"E521")}),1.0]])]});
            extrude(context, id + "F181", {"entities" : qUnion([Q0]), "operationType" : NewBodyOperationType.REMOVE, "endBound" : BoundingType.SYMMETRIC, "oppositeDirection" : true, "depth" : 28.57 * mm, "offsetDistance" : 25.4 * mm});
        }
        {
            var Q0;
            Q0=makeQuery(id+"F33.imprint","IMPRINT",FACE,{"disambiguationData":[TD([[makeQuery(id+"F33.imprint","IMPRINT",EDGE,{"derivedFrom":sQuery(id+"F33.wireOp",EDGE,"E520")}),1.0]])]});
            extrude(context, id + "F182", {"entities" : qUnion([Q0]), "operationType" : NewBodyOperationType.ADD, "endBound" : BoundingType.SYMMETRIC, "oppositeDirection" : true, "depth" : 28.57 * mm, "offsetDistance" : 25.4 * mm});
        }
        {
            var Q0;
            Q0=makeQuery(id+"F33.imprint","IMPRINT",FACE,{"disambiguationData":[TD([[makeQuery(id+"F33.imprint","IMPRINT",EDGE,{"derivedFrom":sQuery(id+"F33.wireOp",EDGE,"E519")}),1.0]])]});
            extrude(context, id + "F183", {"entities" : qUnion([Q0]), "operationType" : NewBodyOperationType.ADD, "endBound" : BoundingType.SYMMETRIC, "oppositeDirection" : true, "depth" : 63.5 * mm, "offsetDistance" : 25.4 * mm});
        }
        {
            var Q0;
            Q0=makeQuery(id+"F22.imprint","IMPRINT",FACE,{"disambiguationData":[TD([[makeQuery(id+"F22.imprint","IMPRINT",EDGE,{"derivedFrom":sQuery(id+"F22.wireOp",EDGE,"E188")}),1.0]])]});
            extrude(context, id + "F184", {"entities" : qUnion([Q0]), "operationType" : NewBodyOperationType.REMOVE, "oppositeDirection" : true, "depth" : 14.29 * mm, "offsetDistance" : 25.4 * mm});
        }
        {
            var Q0;
            Q0=makeQuery(id+"F22.imprint","IMPRINT",FACE,{"disambiguationData":[TD([[makeQuery(id+"F22.imprint","IMPRINT",EDGE,{"derivedFrom":sQuery(id+"F22.wireOp",EDGE,"E243")}),1.0]])]});
            extrude(context, id + "F185", {"entities" : qUnion([Q0]), "oppositeDirection" : true, "depth" : 14.29 * mm, "offsetDistance" : 25.4 * mm});
        }
        {
            var Q0;
            Q0=makeQuery(id+"F22.imprint","IMPRINT",FACE,{"disambiguationData":[TD([[makeQuery(id+"F22.imprint","IMPRINT",EDGE,{"derivedFrom":sQuery(id+"F22.wireOp",EDGE,"E242")}),1.0]])]});
            extrude(context, id + "F186", {"entities" : qUnion([Q0]), "operationType" : NewBodyOperationType.ADD, "oppositeDirection" : true, "depth" : 31.75 * mm, "offsetDistance" : 25.4 * mm});
        }
        {
            var Q0;
            Q0=makeQuery(id+"F33.imprint","IMPRINT",FACE,{"disambiguationData":[TD([[makeQuery(id+"F33.imprint","IMPRINT",EDGE,{"derivedFrom":sQuery(id+"F33.wireOp",EDGE,"E533")}),1.0]])]});
            extrude(context, id + "F187", {"entities" : qUnion([Q0]), "operationType" : NewBodyOperationType.REMOVE, "endBound" : BoundingType.SYMMETRIC, "oppositeDirection" : true, "depth" : 28.57 * mm, "offsetDistance" : 25.4 * mm});
        }
        {
            var Q0;
            Q0=makeQuery(id+"F33.imprint","IMPRINT",FACE,{"disambiguationData":[TD([[makeQuery(id+"F33.imprint","IMPRINT",EDGE,{"derivedFrom":sQuery(id+"F33.wireOp",EDGE,"E532")}),1.0]])]});
            extrude(context, id + "F188", {"entities" : qUnion([Q0]), "operationType" : NewBodyOperationType.ADD, "endBound" : BoundingType.SYMMETRIC, "depth" : 28.57 * mm, "offsetDistance" : 25.4 * mm});
        }
        {
            var Q0;
            Q0=makeQuery(id+"F33.imprint","IMPRINT",FACE,{"disambiguationData":[TD([[makeQuery(id+"F33.imprint","IMPRINT",EDGE,{"derivedFrom":sQuery(id+"F33.wireOp",EDGE,"E531")}),1.0]])]});
            extrude(context, id + "F189", {"entities" : qUnion([Q0]), "operationType" : NewBodyOperationType.ADD, "endBound" : BoundingType.SYMMETRIC, "depth" : 63.5 * mm, "offsetDistance" : 25.4 * mm});
        }
        {
            var Q0;
            Q0=makeQuery(id+"F22.imprint","IMPRINT",FACE,{"disambiguationData":[TD([[makeQuery(id+"F22.imprint","IMPRINT",EDGE,{"derivedFrom":sQuery(id+"F22.wireOp",EDGE,"E244")}),1.0]])]});
            extrude(context, id + "F190", {"entities" : qUnion([Q0]), "operationType" : NewBodyOperationType.REMOVE, "oppositeDirection" : true, "depth" : 14.29 * mm, "offsetDistance" : 25.4 * mm});
        }
        {
            var Q0;
            Q0=makeQuery(id+"F22.imprint","IMPRINT",FACE,{"disambiguationData":[TD([[makeQuery(id+"F22.imprint","IMPRINT",EDGE,{"derivedFrom":sQuery(id+"F22.wireOp",EDGE,"E227")}),1.0]])]});
            extrude(context, id + "F191", {"entities" : qUnion([Q0]), "oppositeDirection" : true, "depth" : 14.29 * mm, "offsetDistance" : 25.4 * mm});
        }
        {
            var Q0;
            Q0=makeQuery(id+"F22.imprint","IMPRINT",FACE,{"disambiguationData":[TD([[makeQuery(id+"F22.imprint","IMPRINT",EDGE,{"derivedFrom":sQuery(id+"F22.wireOp",EDGE,"E226")}),1.0]])]});
            extrude(context, id + "F192", {"entities" : qUnion([Q0]), "operationType" : NewBodyOperationType.ADD, "oppositeDirection" : true, "depth" : 31.75 * mm, "offsetDistance" : 25.4 * mm});
        }
        {
            var Q0;
            Q0=makeQuery(id+"F33.imprint","IMPRINT",FACE,{"disambiguationData":[TD([[makeQuery(id+"F33.imprint","IMPRINT",EDGE,{"derivedFrom":sQuery(id+"F33.wireOp",EDGE,"E517")}),1.0]])]});
            extrude(context, id + "F193", {"entities" : qUnion([Q0]), "operationType" : NewBodyOperationType.REMOVE, "endBound" : BoundingType.SYMMETRIC, "depth" : 28.57 * mm, "offsetDistance" : 25.4 * mm});
        }
        {
            var Q0;
            Q0=makeQuery(id+"F33.imprint","IMPRINT",FACE,{"disambiguationData":[TD([[makeQuery(id+"F33.imprint","IMPRINT",EDGE,{"derivedFrom":sQuery(id+"F33.wireOp",EDGE,"E516")}),1.0]])]});
            extrude(context, id + "F194", {"entities" : qUnion([Q0]), "operationType" : NewBodyOperationType.ADD, "endBound" : BoundingType.SYMMETRIC, "depth" : 28.57 * mm, "offsetDistance" : 25.4 * mm});
        }
        {
            var Q0;
            Q0=makeQuery(id+"F33.imprint","IMPRINT",FACE,{"disambiguationData":[TD([[makeQuery(id+"F33.imprint","IMPRINT",EDGE,{"derivedFrom":sQuery(id+"F33.wireOp",EDGE,"E515")}),1.0]])]});
            extrude(context, id + "F195", {"entities" : qUnion([Q0]), "operationType" : NewBodyOperationType.ADD, "endBound" : BoundingType.SYMMETRIC, "depth" : 63.5 * mm, "offsetDistance" : 25.4 * mm});
        }
        {
            var Q0;
            Q0=makeQuery(id+"F22.imprint","IMPRINT",FACE,{"disambiguationData":[TD([[makeQuery(id+"F22.imprint","IMPRINT",EDGE,{"derivedFrom":sQuery(id+"F22.wireOp",EDGE,"E228")}),1.0]])]});
            extrude(context, id + "F196", {"entities" : qUnion([Q0]), "operationType" : NewBodyOperationType.REMOVE, "oppositeDirection" : true, "depth" : 14.29 * mm, "offsetDistance" : 25.4 * mm});
        }
        {
            var Q0;
            Q0=makeQuery(id+"F22.imprint","IMPRINT",FACE,{"disambiguationData":[TD([[makeQuery(id+"F22.imprint","IMPRINT",EDGE,{"derivedFrom":sQuery(id+"F22.wireOp",EDGE,"E231")}),1.0]])]});
            extrude(context, id + "F197", {"entities" : qUnion([Q0]), "oppositeDirection" : true, "depth" : 14.29 * mm, "offsetDistance" : 25.4 * mm});
        }
        {
            var Q0;
            Q0=makeQuery(id+"F22.imprint","IMPRINT",FACE,{"disambiguationData":[TD([[makeQuery(id+"F22.imprint","IMPRINT",EDGE,{"derivedFrom":sQuery(id+"F22.wireOp",EDGE,"E230")}),1.0]])]});
            extrude(context, id + "F198", {"entities" : qUnion([Q0]), "operationType" : NewBodyOperationType.ADD, "oppositeDirection" : true, "depth" : 25.4 * mm, "offsetDistance" : 25.4 * mm});
        }
        {
            var Q0;
            Q0=makeQuery(id+"F33.imprint","IMPRINT",FACE,{"disambiguationData":[TD([[makeQuery(id+"F33.imprint","IMPRINT",EDGE,{"derivedFrom":sQuery(id+"F33.wireOp",EDGE,"E557")}),1.0]])]});
            extrude(context, id + "F199", {"entities" : qUnion([Q0]), "operationType" : NewBodyOperationType.REMOVE, "endBound" : BoundingType.SYMMETRIC, "depth" : 28.57 * mm, "offsetDistance" : 25.4 * mm});
        }
        {
            var Q0;
            Q0=makeQuery(id+"F33.imprint","IMPRINT",FACE,{"disambiguationData":[TD([[makeQuery(id+"F33.imprint","IMPRINT",EDGE,{"derivedFrom":sQuery(id+"F33.wireOp",EDGE,"E556")}),1.0]])]});
            extrude(context, id + "F200", {"entities" : qUnion([Q0]), "operationType" : NewBodyOperationType.ADD, "endBound" : BoundingType.SYMMETRIC, "depth" : 28.57 * mm, "offsetDistance" : 25.4 * mm});
        }
        {
            var Q0;
            Q0=makeQuery(id+"F33.imprint","IMPRINT",FACE,{"disambiguationData":[TD([[makeQuery(id+"F33.imprint","IMPRINT",EDGE,{"derivedFrom":sQuery(id+"F33.wireOp",EDGE,"E555")}),1.0]])]});
            extrude(context, id + "F201", {"entities" : qUnion([Q0]), "operationType" : NewBodyOperationType.ADD, "endBound" : BoundingType.SYMMETRIC, "depth" : 63.5 * mm, "offsetDistance" : 25.4 * mm});
        }
        {
            var Q0;
            Q0=makeQuery(id+"F22.imprint","IMPRINT",FACE,{"disambiguationData":[TD([[makeQuery(id+"F22.imprint","IMPRINT",EDGE,{"derivedFrom":sQuery(id+"F22.wireOp",EDGE,"E232")}),1.0]])]});
            extrude(context, id + "F202", {"entities" : qUnion([Q0]), "operationType" : NewBodyOperationType.REMOVE, "oppositeDirection" : true, "depth" : 28.57 * mm, "offsetDistance" : 25.4 * mm});
        }
        {
            var Q0;
            Q0=makeQuery(id+"F27.imprint","IMPRINT",FACE,{"disambiguationData":[TD([[makeQuery(id+"F27.imprint","IMPRINT",EDGE,{"derivedFrom":sQuery(id+"F27.wireOp",EDGE,"E356")}),1.0]])]});
            extrude(context, id + "F203", {"entities" : qUnion([Q0]), "depth" : 14.29 * mm, "offsetDistance" : 25.4 * mm});
        }
        {
            var Q0;
            Q0=makeQuery(id+"F27.imprint","IMPRINT",FACE,{"disambiguationData":[TD([[makeQuery(id+"F27.imprint","IMPRINT",EDGE,{"derivedFrom":sQuery(id+"F27.wireOp",EDGE,"E355")}),1.0]])]});
            extrude(context, id + "F204", {"entities" : qUnion([Q0]), "operationType" : NewBodyOperationType.ADD, "depth" : 31.75 * mm, "offsetDistance" : 25.4 * mm});
        }
        {
            var Q0;
            Q0=makeQuery(id+"F15.imprint","IMPRINT",FACE,{"disambiguationData":[TD([[makeQuery(id+"F15.imprint","IMPRINT",EDGE,{"derivedFrom":sQuery(id+"F15.wireOp",EDGE,"E114")}),1.0]])]});
            extrude(context, id + "F205", {"entities" : qUnion([Q0]), "operationType" : NewBodyOperationType.ADD, "depth" : 14.29 * mm, "offsetDistance" : 25.4 * mm});
        }
        {
            var Q0;
            Q0=makeQuery(id+"F15.imprint","IMPRINT",FACE,{"disambiguationData":[TD([[makeQuery(id+"F15.imprint","IMPRINT",EDGE,{"derivedFrom":sQuery(id+"F15.wireOp",EDGE,"E113")}),1.0]])]});
            extrude(context, id + "F206", {"entities" : qUnion([Q0]), "operationType" : NewBodyOperationType.ADD, "depth" : 31.75 * mm, "offsetDistance" : 25.4 * mm});
        }
    });
